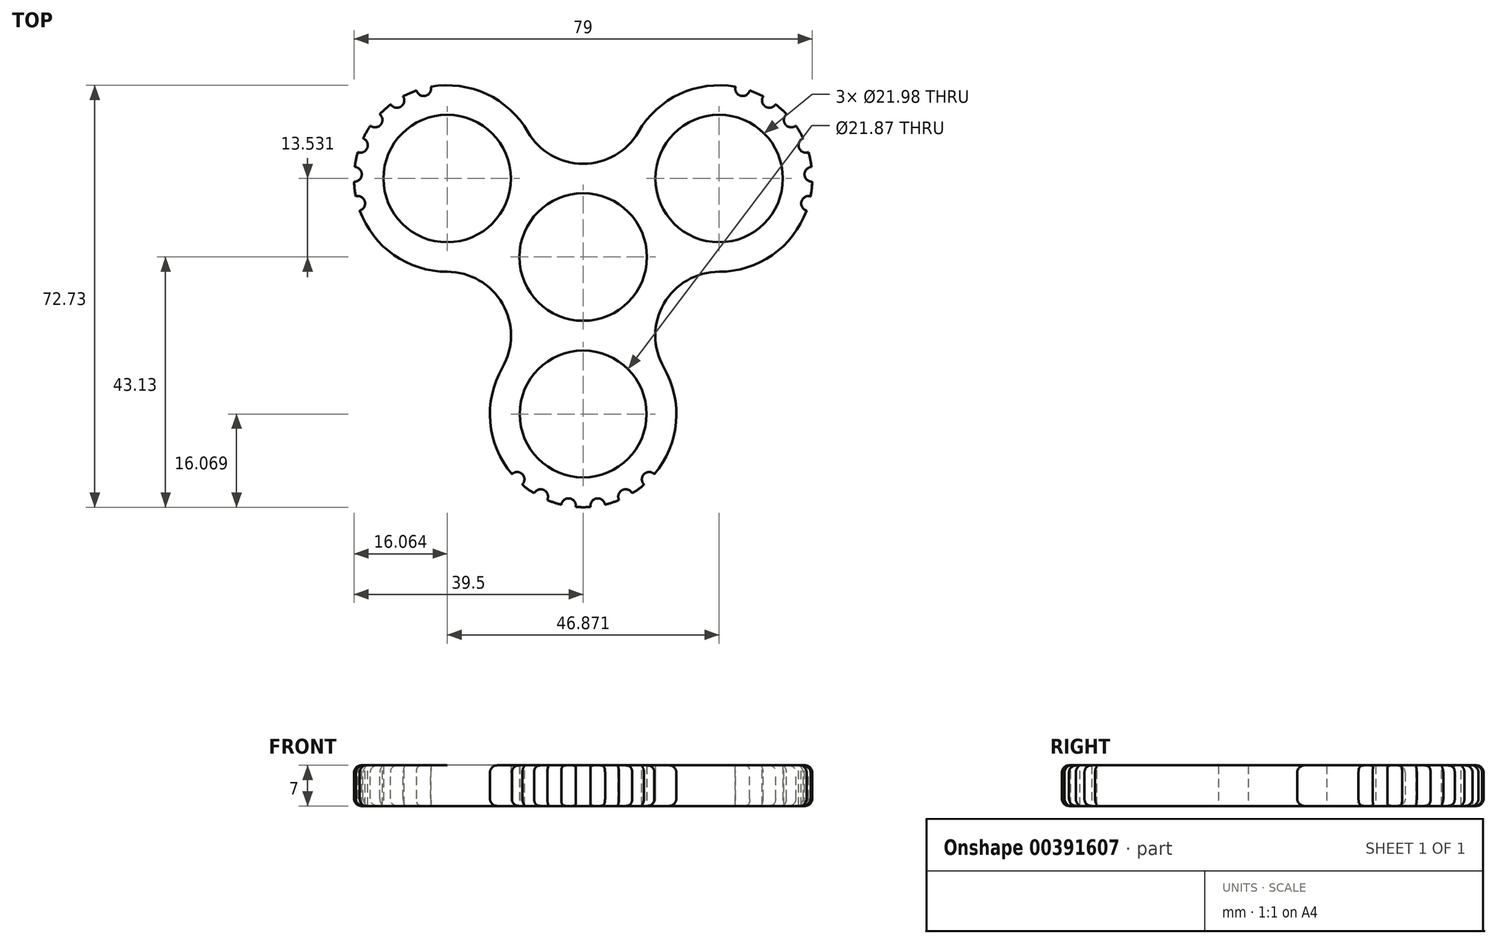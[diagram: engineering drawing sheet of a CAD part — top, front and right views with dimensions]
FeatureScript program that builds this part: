
annotation { "Feature Type Name" : "Feature", "Feature Type Description" : "" }
export const myFeature = defineFeature(function(context is Context, id is Id, definition is map)
    precondition{}
    {
        {
            var Q0;
            Q0=qCreatedBy(makeId("Top.planeOp"),FACE);
            var sketch = newSketch(context, id + "F0", { "sketchPlane" : qUnion([Q0])});
            skArc(sketch, "E0", {"start": v(0, 11) * mm, "mid": v(-5.5, -9.52) * mm, "end": v(9.52, 5.5) * mm, "construction": true});
            skLineSegment(sketch, "E1", {"start": v(0, 0) * mm, "end": v(92.12, 53.18) * mm, "construction": true});
            skLineSegment(sketch, "E2", {"start": v(0, 0) * mm, "end": v(-9.52, 5.5) * mm, "construction": true});
            skLineSegment(sketch, "E3", {"start": v(0, 0) * mm, "end": v(0, -70.87) * mm, "construction": true});
            skCircle(sketch, "E4", {"center": v(-23.44, 13.53) * mm, "radius": 11 * mm, "construction": true});
            skArc(sketch, "E5", {"start": v(13.92, 8.04) * mm, "mid": v(28.93, 4.01) * mm, "end": v(32.95, 19.03) * mm, "construction": true});
            skCircle(sketch, "E6", {"center": v(0, -27.06) * mm, "radius": 11 * mm, "construction": true});
            skLineSegment(sketch, "E7", {"start": v(0, 0) * mm, "end": v(-69.62, -40.2) * mm, "construction": true});
            skLineSegment(sketch, "E8", {"start": v(0, 0) * mm, "end": v(71.9, -41.52) * mm, "construction": true});
            skLineSegment(sketch, "E9", {"start": v(0, 0) * mm, "end": v(0, 11) * mm, "construction": true});
            skLineSegment(sketch, "E10", {"start": v(-23.44, 13.53) * mm, "end": v(-12.14, 33.1) * mm, "construction": true});
            skLineSegment(sketch, "E11", {"start": v(23.44, 13.53) * mm, "end": v(12.02, 33.3) * mm, "construction": true});
            skLineSegment(sketch, "E12", {"start": v(-37.35, 21.57) * mm, "end": v(-32.95, 19.03) * mm, "construction": true});
            skLineSegment(sketch, "E13", {"start": v(9.52, 5.5) * mm, "end": v(13.92, 8.04) * mm});
            skLineSegment(sketch, "E14", {"start": v(37.35, 21.57) * mm, "end": v(32.95, 19.03) * mm});
            skArc(sketch, "E15", {"start": v(-9.52, 5.5) * mm, "mid": v(-5.5, 9.52) * mm, "end": v(0, 11) * mm});
            skArc(sketch, "E16", {"start": v(-9.52, 21.57) * mm, "mid": v(-5.5, 17.54) * mm, "end": v(0, 16.07) * mm});
            skArc(sketch, "E17", {"start": v(-32.95, 19.03) * mm, "mid": v(-17.94, 23.05) * mm, "end": v(-13.92, 8.04) * mm});
            skLineSegment(sketch, "E18.trimOffspring", {"start": v(-37.35, 21.57) * mm, "end": v(-92.12, 53.18) * mm, "construction": true});
            skLineSegment(sketch, "E19.trimOffspring", {"start": v(-13.92, 8.04) * mm, "end": v(-32.95, 19.03) * mm, "construction": true});
            skArc(sketch, "E20", {"start": v(-9.52, 21.57) * mm, "mid": v(-23.44, 29.6) * mm, "end": v(-37.35, 21.57) * mm});
            skLineSegment(sketch, "E21", {"start": v(-37.35, 21.57) * mm, "end": v(-32.95, 19.03) * mm});
            skLineSegment(sketch, "E22", {"start": v(-13.92, 8.04) * mm, "end": v(-9.52, 5.5) * mm});
            skPoint(sketch, "E23.start.orphan", {"position": v(23.44, 29.6) * mm});
            skLineSegment(sketch, "E24.trimOffspring", {"start": v(0, 16.07) * mm, "end": v(0, 62.86) * mm, "construction": true});
            skLineSegment(sketch, "E25", {"start": v(0, 16.07) * mm, "end": v(0, 11) * mm});
            skLineSegment(sketch, "E26.MirrorCS", {"start": v(-13.92, -8.04) * mm, "end": v(-9.52, -5.5) * mm});
            skArc(sketch, "E27.MirrorCS", {"start": v(-23.44, -2.54) * mm, "mid": v(-17.94, -4.01) * mm, "end": v(-13.92, -8.04) * mm});
            skArc(sketch, "E28.MirrorCS", {"start": v(-23.44, -2.54) * mm, "mid": v(-37.35, 5.5) * mm, "end": v(-37.35, 21.57) * mm});
            skArc(sketch, "E29.MirrorCS", {"start": v(-9.52, 5.5) * mm, "mid": v(-11, 0) * mm, "end": v(-9.52, -5.5) * mm});
            skArc(sketch, "E30.MirrorCS", {"start": v(-32.95, 19.03) * mm, "mid": v(-28.93, 4.01) * mm, "end": v(-13.92, 8.04) * mm});
            skArc(sketch, "E31.MirrorCS", {"start": v(23.44, -2.54) * mm, "mid": v(37.35, 5.5) * mm, "end": v(37.35, 21.57) * mm});
            skLineSegment(sketch, "E32.MirrorCS", {"start": v(13.92, 8.04) * mm, "end": v(9.52, 5.5) * mm});
            skArc(sketch, "E33.MirrorCS", {"start": v(32.95, 19.03) * mm, "mid": v(17.94, 23.05) * mm, "end": v(13.92, 8.04) * mm});
            skArc(sketch, "E34.MirrorCS", {"start": v(32.95, 19.03) * mm, "mid": v(28.93, 4.01) * mm, "end": v(13.92, 8.04) * mm});
            skLineSegment(sketch, "E35.MirrorCS", {"start": v(13.92, -8.04) * mm, "end": v(9.52, -5.5) * mm});
            skArc(sketch, "E36.MirrorCS", {"start": v(23.44, -2.54) * mm, "mid": v(17.94, -4.01) * mm, "end": v(13.92, -8.04) * mm});
            skLineSegment(sketch, "E37.MirrorCS", {"start": v(37.35, 21.57) * mm, "end": v(32.95, 19.03) * mm, "construction": true});
            skArc(sketch, "E38.MirrorCS", {"start": v(9.52, 5.5) * mm, "mid": v(11, 0) * mm, "end": v(9.52, -5.5) * mm});
            skArc(sketch, "E39.MirrorCS", {"start": v(9.52, 21.57) * mm, "mid": v(23.44, 29.6) * mm, "end": v(37.35, 21.57) * mm});
            skLineSegment(sketch, "E40.MirrorCS", {"start": v(23.44, 13.53) * mm, "end": v(12.14, 33.1) * mm, "construction": true});
            skLineSegment(sketch, "E41.MirrorCS", {"start": v(0, 0) * mm, "end": v(9.52, 5.5) * mm, "construction": true});
            skArc(sketch, "E42.MirrorCS", {"start": v(9.52, 5.5) * mm, "mid": v(5.5, 9.52) * mm, "end": v(0, 11) * mm});
            skArc(sketch, "E43.MirrorCS", {"start": v(9.52, 21.57) * mm, "mid": v(5.5, 17.54) * mm, "end": v(0, 16.07) * mm});
            skCircle(sketch, "E44.MirrorC", {"center": v(23.44, 13.53) * mm, "radius": 11 * mm, "construction": true});
            skLineSegment(sketch, "E45.MirrorCS", {"start": v(13.92, 8.04) * mm, "end": v(32.95, 19.03) * mm, "construction": true});
            skArc(sketch, "E46", {"start": v(-9.52, -5.5) * mm, "mid": v(0, -11) * mm, "end": v(9.52, -5.5) * mm});
            skArc(sketch, "E47.MirrorCS", {"start": v(-13.92, -19.03) * mm, "mid": v(-12.45, -13.53) * mm, "end": v(-13.92, -8.04) * mm});
            skArc(sketch, "E48.MirrorCS", {"start": v(-13.92, -19.03) * mm, "mid": v(-13.92, -35.1) * mm, "end": v(0, -43.13) * mm});
            skArc(sketch, "E49.MirrorCS", {"start": v(13.92, -19.03) * mm, "mid": v(12.45, -13.53) * mm, "end": v(13.92, -8.04) * mm});
            skArc(sketch, "E50.MirrorCS", {"start": v(13.92, -19.03) * mm, "mid": v(13.92, -35.1) * mm, "end": v(0, -43.13) * mm});
            skCircle(sketch, "E51", {"center": v(0, -27.06) * mm, "radius": 10.94 * mm});
            skSolve(sketch);
        }
        {
            var Q0;
            Q0 = qSketchRegion(id + "F0", true);
            extrude(context, id + "F1", {"entities" : qUnion([Q0]), "depth" : 7 * mm});
        }
        {
            var Q0;
            Q0=makeQuery(id+"F1.opExtrude","CAP_FACE",FACE,{"disambiguationData":[OSD([sQuery(id+"F0.wireOp",EDGE,"E15"),sQuery(id+"F0.wireOp",EDGE,"E16"),sQuery(id+"F0.wireOp",EDGE,"E17"),sQuery(id+"F0.wireOp",EDGE,"E20"),sQuery(id+"F0.wireOp",EDGE,"E27.MirrorCS"),sQuery(id+"F0.wireOp",EDGE,"E29.MirrorCS"),sQuery(id+"F0.wireOp",EDGE,"E30.MirrorCS"),sQuery(id+"F0.wireOp",EDGE,"E28.MirrorCS"),sQuery(id+"F0.wireOp",EDGE,"E33.MirrorCS"),sQuery(id+"F0.wireOp",EDGE,"E34.MirrorCS"),sQuery(id+"F0.wireOp",EDGE,"E31.MirrorCS"),sQuery(id+"F0.wireOp",EDGE,"E36.MirrorCS"),sQuery(id+"F0.wireOp",EDGE,"E38.MirrorCS"),sQuery(id+"F0.wireOp",EDGE,"E39.MirrorCS"),sQuery(id+"F0.wireOp",EDGE,"E42.MirrorCS"),sQuery(id+"F0.wireOp",EDGE,"E43.MirrorCS"),sQuery(id+"F0.wireOp",EDGE,"E46"),sQuery(id+"F0.wireOp",EDGE,"E47.MirrorCS"),sQuery(id+"F0.wireOp",EDGE,"E48.MirrorCS"),sQuery(id+"F0.wireOp",EDGE,"E49.MirrorCS"),sQuery(id+"F0.wireOp",EDGE,"E50.MirrorCS"),sQuery(id+"F0.wireOp",EDGE,"E51")])],"isStart":false});
            var sketch = newSketch(context, id + "F2", { "sketchPlane" : qUnion([Q0])});
            skArc(sketch, "E52", {"start": v(-36.68, 22.64) * mm, "mid": v(-34.89, 22.83) * mm, "end": v(-35.07, 24.61) * mm});
            skArc(sketch, "E53", {"start": v(-38.85, 18.07) * mm, "mid": v(-37.21, 18.8) * mm, "end": v(-37.94, 20.44) * mm});
            skArc(sketch, "E54", {"start": v(-36.68, 22.64) * mm, "mid": v(-35.91, 23.66) * mm, "end": v(-35.07, 24.61) * mm});
            skArc(sketch, "E55", {"start": v(-38.85, 18.07) * mm, "mid": v(-38.45, 19.27) * mm, "end": v(-37.94, 20.44) * mm});
            skArc(sketch, "E56", {"start": v(-39.5, 12.99) * mm, "mid": v(-38.17, 14.2) * mm, "end": v(-39.38, 15.53) * mm});
            skArc(sketch, "E57", {"start": v(-33.18, 26.3) * mm, "mid": v(-31.43, 25.93) * mm, "end": v(-31.05, 27.68) * mm});
            skArc(sketch, "E58", {"start": v(-33.18, 26.3) * mm, "mid": v(-32.14, 27.04) * mm, "end": v(-31.05, 27.68) * mm});
            skArc(sketch, "E59", {"start": v(-39.5, 12.99) * mm, "mid": v(-39.49, 14.26) * mm, "end": v(-39.38, 15.53) * mm});
            skArc(sketch, "E60", {"start": v(-38.53, 8.02) * mm, "mid": v(-37.65, 9.58) * mm, "end": v(-39.21, 10.47) * mm});
            skArc(sketch, "E61", {"start": v(-28.72, 28.7) * mm, "mid": v(-27.17, 27.8) * mm, "end": v(-26.27, 29.35) * mm});
            skArc(sketch, "E62", {"start": v(-28.72, 28.7) * mm, "mid": v(-27.5, 29.08) * mm, "end": v(-26.27, 29.35) * mm});
            skArc(sketch, "E63", {"start": v(-38.53, 8.02) * mm, "mid": v(-38.92, 9.23) * mm, "end": v(-39.21, 10.47) * mm});
            skLineSegment(sketch, "E64", {"start": v(0, 53.35) * mm, "end": v(0, -27.06) * mm, "construction": true});
            skArc(sketch, "E65.MirrorCS", {"start": v(28.72, 28.7) * mm, "mid": v(27.17, 27.8) * mm, "end": v(26.27, 29.35) * mm});
            skArc(sketch, "E66.MirrorCS", {"start": v(28.72, 28.7) * mm, "mid": v(27.5, 29.08) * mm, "end": v(26.27, 29.35) * mm});
            skArc(sketch, "E67.MirrorCS", {"start": v(33.18, 26.3) * mm, "mid": v(31.43, 25.93) * mm, "end": v(31.05, 27.68) * mm});
            skArc(sketch, "E68.MirrorCS", {"start": v(33.18, 26.3) * mm, "mid": v(32.14, 27.04) * mm, "end": v(31.05, 27.68) * mm});
            skArc(sketch, "E69.MirrorCS", {"start": v(36.68, 22.64) * mm, "mid": v(34.89, 22.83) * mm, "end": v(35.07, 24.61) * mm});
            skArc(sketch, "E70.MirrorCS", {"start": v(38.85, 18.07) * mm, "mid": v(37.21, 18.8) * mm, "end": v(37.94, 20.44) * mm});
            skArc(sketch, "E71.MirrorCS", {"start": v(39.5, 12.99) * mm, "mid": v(38.17, 14.2) * mm, "end": v(39.38, 15.53) * mm});
            skArc(sketch, "E72.MirrorCS", {"start": v(38.53, 8.02) * mm, "mid": v(37.65, 9.58) * mm, "end": v(39.21, 10.47) * mm});
            skArc(sketch, "E73.MirrorCS", {"start": v(36.68, 22.64) * mm, "mid": v(35.91, 23.66) * mm, "end": v(35.07, 24.61) * mm});
            skArc(sketch, "E74.MirrorCS", {"start": v(38.85, 18.07) * mm, "mid": v(38.45, 19.27) * mm, "end": v(37.94, 20.44) * mm});
            skArc(sketch, "E75.MirrorCS", {"start": v(39.5, 12.99) * mm, "mid": v(39.49, 14.26) * mm, "end": v(39.38, 15.53) * mm});
            skArc(sketch, "E76.MirrorCS", {"start": v(38.53, 8.02) * mm, "mid": v(38.92, 9.23) * mm, "end": v(39.21, 10.47) * mm});
            skArc(sketch, "E77", {"start": v(3.78, -42.68) * mm, "mid": v(2.32, -41.63) * mm, "end": v(1.27, -43.08) * mm});
            skArc(sketch, "E78", {"start": v(8.45, -40.73) * mm, "mid": v(6.74, -40.18) * mm, "end": v(6.2, -41.9) * mm});
            skArc(sketch, "E79", {"start": v(12.28, -37.42) * mm, "mid": v(10.49, -37.43) * mm, "end": v(10.5, -39.23) * mm});
            skArc(sketch, "E80", {"start": v(-1.27, -43.08) * mm, "mid": v(-2.32, -41.63) * mm, "end": v(-3.78, -42.68) * mm});
            skArc(sketch, "E81", {"start": v(-6.2, -41.9) * mm, "mid": v(-6.74, -40.18) * mm, "end": v(-8.45, -40.73) * mm});
            skArc(sketch, "E82", {"start": v(-10.5, -39.23) * mm, "mid": v(-10.49, -37.43) * mm, "end": v(-12.28, -37.42) * mm});
            skArc(sketch, "E83", {"start": v(12.28, -37.42) * mm, "mid": v(11.43, -38.36) * mm, "end": v(10.5, -39.23) * mm});
            skArc(sketch, "E84", {"start": v(8.45, -40.73) * mm, "mid": v(7.34, -41.36) * mm, "end": v(6.2, -41.9) * mm});
            skArc(sketch, "E85", {"start": v(3.78, -42.68) * mm, "mid": v(2.53, -42.93) * mm, "end": v(1.27, -43.08) * mm});
            skArc(sketch, "E86", {"start": v(-1.27, -43.08) * mm, "mid": v(-2.53, -42.93) * mm, "end": v(-3.78, -42.68) * mm});
            skArc(sketch, "E87", {"start": v(-6.2, -41.9) * mm, "mid": v(-7.34, -41.36) * mm, "end": v(-8.45, -40.73) * mm});
            skArc(sketch, "E88", {"start": v(-10.5, -39.23) * mm, "mid": v(-11.43, -38.36) * mm, "end": v(-12.28, -37.42) * mm});
            skSolve(sketch);
        }
        {
            var Q0;
            Q0 = qSketchRegion(id + "F2", true);
            extrude(context, id + "F3", {"entities" : qUnion([Q0]), "operationType" : NewBodyOperationType.REMOVE, "endBound" : BoundingType.THROUGH_ALL, "oppositeDirection" : true, "depth" : 25.4 * mm});
        }
        {
            var Q0;
            {var subQ0=sQuery(id+"F0.wireOp",EDGE,"E47.MirrorCS");var subQ1=sQuery(id+"F0.wireOp",EDGE,"E28.MirrorCS");var subQ2=sQuery(id+"F0.wireOp",EDGE,"E27.MirrorCS");var subQ3=sQuery(id+"F0.wireOp",EDGE,"E20");Q0=makeQuery(id+"F3.boolean.opBoolean","SPLIT",EDGE,{"disambiguationData":[TD([makeQuery(id+"F1.opExtrude","CAP_FACE",FACE,{"disambiguationData":[OSD([sQuery(id+"F0.wireOp",EDGE,"E15"),sQuery(id+"F0.wireOp",EDGE,"E16"),sQuery(id+"F0.wireOp",EDGE,"E17"),subQ3,subQ2,sQuery(id+"F0.wireOp",EDGE,"E29.MirrorCS"),sQuery(id+"F0.wireOp",EDGE,"E30.MirrorCS"),subQ1,sQuery(id+"F0.wireOp",EDGE,"E33.MirrorCS"),sQuery(id+"F0.wireOp",EDGE,"E34.MirrorCS"),sQuery(id+"F0.wireOp",EDGE,"E31.MirrorCS"),sQuery(id+"F0.wireOp",EDGE,"E36.MirrorCS"),sQuery(id+"F0.wireOp",EDGE,"E38.MirrorCS"),sQuery(id+"F0.wireOp",EDGE,"E39.MirrorCS"),sQuery(id+"F0.wireOp",EDGE,"E42.MirrorCS"),sQuery(id+"F0.wireOp",EDGE,"E43.MirrorCS"),sQuery(id+"F0.wireOp",EDGE,"E46"),subQ0,sQuery(id+"F0.wireOp",EDGE,"E48.MirrorCS"),sQuery(id+"F0.wireOp",EDGE,"E49.MirrorCS"),sQuery(id+"F0.wireOp",EDGE,"E50.MirrorCS"),sQuery(id+"F0.wireOp",EDGE,"E51")])],"isStart":false}),makeQuery(id+"F1.opExtrude","SWEPT_FACE",FACE,{"disambiguationData":[OSD([subQ3,subQ1])]}),makeQuery(id+"F1.opExtrude","SWEPT_FACE",FACE,{"disambiguationData":[OSD([subQ2,subQ0])]}),makeQuery(id+"F3.opExtrude","SWEPT_FACE",FACE,{"disambiguationData":[OSD([sQuery(id+"F2.wireOp",EDGE,"E60")])]})])],"derivedFrom":makeQuery(id+"F1.opExtrude","CAP_EDGE",EDGE,{"disambiguationData":[OSD([subQ3,subQ1])],"isStart":false})});}
            var Q1;
            Q1=makeQuery(id+"F1.opExtrude","CAP_EDGE",EDGE,{"disambiguationData":[OSD([sQuery(id+"F0.wireOp",EDGE,"E27.MirrorCS"),sQuery(id+"F0.wireOp",EDGE,"E47.MirrorCS")])],"isStart":false});
            var Q2;
            {var subQ0=sQuery(id+"F0.wireOp",EDGE,"E50.MirrorCS");var subQ1=sQuery(id+"F0.wireOp",EDGE,"E48.MirrorCS");var subQ2=sQuery(id+"F0.wireOp",EDGE,"E47.MirrorCS");var subQ3=sQuery(id+"F0.wireOp",EDGE,"E27.MirrorCS");Q2=makeQuery(id+"F3.boolean.opBoolean","SPLIT",EDGE,{"disambiguationData":[TD([makeQuery(id+"F1.opExtrude","CAP_FACE",FACE,{"disambiguationData":[OSD([sQuery(id+"F0.wireOp",EDGE,"E15"),sQuery(id+"F0.wireOp",EDGE,"E16"),sQuery(id+"F0.wireOp",EDGE,"E17"),sQuery(id+"F0.wireOp",EDGE,"E20"),subQ3,sQuery(id+"F0.wireOp",EDGE,"E29.MirrorCS"),sQuery(id+"F0.wireOp",EDGE,"E30.MirrorCS"),sQuery(id+"F0.wireOp",EDGE,"E28.MirrorCS"),sQuery(id+"F0.wireOp",EDGE,"E33.MirrorCS"),sQuery(id+"F0.wireOp",EDGE,"E34.MirrorCS"),sQuery(id+"F0.wireOp",EDGE,"E31.MirrorCS"),sQuery(id+"F0.wireOp",EDGE,"E36.MirrorCS"),sQuery(id+"F0.wireOp",EDGE,"E38.MirrorCS"),sQuery(id+"F0.wireOp",EDGE,"E39.MirrorCS"),sQuery(id+"F0.wireOp",EDGE,"E42.MirrorCS"),sQuery(id+"F0.wireOp",EDGE,"E43.MirrorCS"),sQuery(id+"F0.wireOp",EDGE,"E46"),subQ2,subQ1,sQuery(id+"F0.wireOp",EDGE,"E49.MirrorCS"),subQ0,sQuery(id+"F0.wireOp",EDGE,"E51")])],"isStart":false}),makeQuery(id+"F1.opExtrude","SWEPT_FACE",FACE,{"disambiguationData":[OSD([subQ3,subQ2])]}),makeQuery(id+"F1.opExtrude","SWEPT_FACE",FACE,{"disambiguationData":[OSD([subQ1,subQ0])]}),makeQuery(id+"F3.opExtrude","SWEPT_FACE",FACE,{"disambiguationData":[OSD([sQuery(id+"F2.wireOp",EDGE,"E82")])]})])],"derivedFrom":makeQuery(id+"F1.opExtrude","CAP_EDGE",EDGE,{"disambiguationData":[OSD([subQ1,subQ0])],"isStart":false})});}
            var Q3;
            {var subQ0=sQuery(id+"F0.wireOp",EDGE,"E50.MirrorCS");var subQ1=sQuery(id+"F0.wireOp",EDGE,"E49.MirrorCS");var subQ2=sQuery(id+"F0.wireOp",EDGE,"E48.MirrorCS");var subQ3=sQuery(id+"F0.wireOp",EDGE,"E36.MirrorCS");Q3=makeQuery(id+"F3.boolean.opBoolean","SPLIT",EDGE,{"disambiguationData":[TD([makeQuery(id+"F1.opExtrude","CAP_FACE",FACE,{"disambiguationData":[OSD([sQuery(id+"F0.wireOp",EDGE,"E15"),sQuery(id+"F0.wireOp",EDGE,"E16"),sQuery(id+"F0.wireOp",EDGE,"E17"),sQuery(id+"F0.wireOp",EDGE,"E20"),sQuery(id+"F0.wireOp",EDGE,"E27.MirrorCS"),sQuery(id+"F0.wireOp",EDGE,"E29.MirrorCS"),sQuery(id+"F0.wireOp",EDGE,"E30.MirrorCS"),sQuery(id+"F0.wireOp",EDGE,"E28.MirrorCS"),sQuery(id+"F0.wireOp",EDGE,"E33.MirrorCS"),sQuery(id+"F0.wireOp",EDGE,"E34.MirrorCS"),sQuery(id+"F0.wireOp",EDGE,"E31.MirrorCS"),subQ3,sQuery(id+"F0.wireOp",EDGE,"E38.MirrorCS"),sQuery(id+"F0.wireOp",EDGE,"E39.MirrorCS"),sQuery(id+"F0.wireOp",EDGE,"E42.MirrorCS"),sQuery(id+"F0.wireOp",EDGE,"E43.MirrorCS"),sQuery(id+"F0.wireOp",EDGE,"E46"),sQuery(id+"F0.wireOp",EDGE,"E47.MirrorCS"),subQ2,subQ1,subQ0,sQuery(id+"F0.wireOp",EDGE,"E51")])],"isStart":false}),makeQuery(id+"F1.opExtrude","SWEPT_FACE",FACE,{"disambiguationData":[OSD([subQ3,subQ1])]}),makeQuery(id+"F1.opExtrude","SWEPT_FACE",FACE,{"disambiguationData":[OSD([subQ2,subQ0])]}),makeQuery(id+"F3.opExtrude","SWEPT_FACE",FACE,{"disambiguationData":[OSD([sQuery(id+"F2.wireOp",EDGE,"E79")])]})])],"derivedFrom":makeQuery(id+"F1.opExtrude","CAP_EDGE",EDGE,{"disambiguationData":[OSD([subQ2,subQ0])],"isStart":false})});}
            var Q4;
            Q4=makeQuery(id+"F1.opExtrude","CAP_EDGE",EDGE,{"disambiguationData":[OSD([sQuery(id+"F0.wireOp",EDGE,"E36.MirrorCS"),sQuery(id+"F0.wireOp",EDGE,"E49.MirrorCS")])],"isStart":false});
            var Q5;
            {var subQ0=sQuery(id+"F0.wireOp",EDGE,"E49.MirrorCS");var subQ1=sQuery(id+"F0.wireOp",EDGE,"E39.MirrorCS");var subQ2=sQuery(id+"F0.wireOp",EDGE,"E36.MirrorCS");var subQ3=sQuery(id+"F0.wireOp",EDGE,"E31.MirrorCS");Q5=makeQuery(id+"F3.boolean.opBoolean","SPLIT",EDGE,{"disambiguationData":[TD([makeQuery(id+"F1.opExtrude","CAP_FACE",FACE,{"disambiguationData":[OSD([sQuery(id+"F0.wireOp",EDGE,"E15"),sQuery(id+"F0.wireOp",EDGE,"E16"),sQuery(id+"F0.wireOp",EDGE,"E17"),sQuery(id+"F0.wireOp",EDGE,"E20"),sQuery(id+"F0.wireOp",EDGE,"E27.MirrorCS"),sQuery(id+"F0.wireOp",EDGE,"E29.MirrorCS"),sQuery(id+"F0.wireOp",EDGE,"E30.MirrorCS"),sQuery(id+"F0.wireOp",EDGE,"E28.MirrorCS"),sQuery(id+"F0.wireOp",EDGE,"E33.MirrorCS"),sQuery(id+"F0.wireOp",EDGE,"E34.MirrorCS"),subQ3,subQ2,sQuery(id+"F0.wireOp",EDGE,"E38.MirrorCS"),subQ1,sQuery(id+"F0.wireOp",EDGE,"E42.MirrorCS"),sQuery(id+"F0.wireOp",EDGE,"E43.MirrorCS"),sQuery(id+"F0.wireOp",EDGE,"E46"),sQuery(id+"F0.wireOp",EDGE,"E47.MirrorCS"),sQuery(id+"F0.wireOp",EDGE,"E48.MirrorCS"),subQ0,sQuery(id+"F0.wireOp",EDGE,"E50.MirrorCS"),sQuery(id+"F0.wireOp",EDGE,"E51")])],"isStart":false}),makeQuery(id+"F1.opExtrude","SWEPT_FACE",FACE,{"disambiguationData":[OSD([subQ3,subQ1])]}),makeQuery(id+"F1.opExtrude","SWEPT_FACE",FACE,{"disambiguationData":[OSD([subQ2,subQ0])]}),makeQuery(id+"F3.opExtrude","SWEPT_FACE",FACE,{"disambiguationData":[OSD([sQuery(id+"F2.wireOp",EDGE,"E72.MirrorCS")])]})])],"derivedFrom":makeQuery(id+"F1.opExtrude","CAP_EDGE",EDGE,{"disambiguationData":[OSD([subQ3,subQ1])],"isStart":false})});}
            var Q6;
            {var subQ0=sQuery(id+"F0.wireOp",EDGE,"E43.MirrorCS");var subQ1=sQuery(id+"F0.wireOp",EDGE,"E39.MirrorCS");var subQ2=sQuery(id+"F0.wireOp",EDGE,"E31.MirrorCS");var subQ3=sQuery(id+"F0.wireOp",EDGE,"E16");Q6=makeQuery(id+"F3.boolean.opBoolean","SPLIT",EDGE,{"disambiguationData":[TD([makeQuery(id+"F1.opExtrude","CAP_FACE",FACE,{"disambiguationData":[OSD([sQuery(id+"F0.wireOp",EDGE,"E15"),subQ3,sQuery(id+"F0.wireOp",EDGE,"E17"),sQuery(id+"F0.wireOp",EDGE,"E20"),sQuery(id+"F0.wireOp",EDGE,"E27.MirrorCS"),sQuery(id+"F0.wireOp",EDGE,"E29.MirrorCS"),sQuery(id+"F0.wireOp",EDGE,"E30.MirrorCS"),sQuery(id+"F0.wireOp",EDGE,"E28.MirrorCS"),sQuery(id+"F0.wireOp",EDGE,"E33.MirrorCS"),sQuery(id+"F0.wireOp",EDGE,"E34.MirrorCS"),subQ2,sQuery(id+"F0.wireOp",EDGE,"E36.MirrorCS"),sQuery(id+"F0.wireOp",EDGE,"E38.MirrorCS"),subQ1,sQuery(id+"F0.wireOp",EDGE,"E42.MirrorCS"),subQ0,sQuery(id+"F0.wireOp",EDGE,"E46"),sQuery(id+"F0.wireOp",EDGE,"E47.MirrorCS"),sQuery(id+"F0.wireOp",EDGE,"E48.MirrorCS"),sQuery(id+"F0.wireOp",EDGE,"E49.MirrorCS"),sQuery(id+"F0.wireOp",EDGE,"E50.MirrorCS"),sQuery(id+"F0.wireOp",EDGE,"E51")])],"isStart":false}),makeQuery(id+"F1.opExtrude","SWEPT_FACE",FACE,{"disambiguationData":[OSD([subQ3,subQ0])]}),makeQuery(id+"F1.opExtrude","SWEPT_FACE",FACE,{"disambiguationData":[OSD([subQ2,subQ1])]}),makeQuery(id+"F3.opExtrude","SWEPT_FACE",FACE,{"disambiguationData":[OSD([sQuery(id+"F2.wireOp",EDGE,"E65.MirrorCS")])]})])],"derivedFrom":makeQuery(id+"F1.opExtrude","CAP_EDGE",EDGE,{"disambiguationData":[OSD([subQ2,subQ1])],"isStart":false})});}
            var Q7;
            Q7=makeQuery(id+"F1.opExtrude","CAP_EDGE",EDGE,{"disambiguationData":[OSD([sQuery(id+"F0.wireOp",EDGE,"E16"),sQuery(id+"F0.wireOp",EDGE,"E43.MirrorCS")])],"isStart":false});
            var Q8;
            {var subQ0=sQuery(id+"F0.wireOp",EDGE,"E43.MirrorCS");var subQ1=sQuery(id+"F0.wireOp",EDGE,"E28.MirrorCS");var subQ2=sQuery(id+"F0.wireOp",EDGE,"E20");var subQ3=sQuery(id+"F0.wireOp",EDGE,"E16");Q8=makeQuery(id+"F3.boolean.opBoolean","SPLIT",EDGE,{"disambiguationData":[TD([makeQuery(id+"F1.opExtrude","CAP_FACE",FACE,{"disambiguationData":[OSD([sQuery(id+"F0.wireOp",EDGE,"E15"),subQ3,sQuery(id+"F0.wireOp",EDGE,"E17"),subQ2,sQuery(id+"F0.wireOp",EDGE,"E27.MirrorCS"),sQuery(id+"F0.wireOp",EDGE,"E29.MirrorCS"),sQuery(id+"F0.wireOp",EDGE,"E30.MirrorCS"),subQ1,sQuery(id+"F0.wireOp",EDGE,"E33.MirrorCS"),sQuery(id+"F0.wireOp",EDGE,"E34.MirrorCS"),sQuery(id+"F0.wireOp",EDGE,"E31.MirrorCS"),sQuery(id+"F0.wireOp",EDGE,"E36.MirrorCS"),sQuery(id+"F0.wireOp",EDGE,"E38.MirrorCS"),sQuery(id+"F0.wireOp",EDGE,"E39.MirrorCS"),sQuery(id+"F0.wireOp",EDGE,"E42.MirrorCS"),subQ0,sQuery(id+"F0.wireOp",EDGE,"E46"),sQuery(id+"F0.wireOp",EDGE,"E47.MirrorCS"),sQuery(id+"F0.wireOp",EDGE,"E48.MirrorCS"),sQuery(id+"F0.wireOp",EDGE,"E49.MirrorCS"),sQuery(id+"F0.wireOp",EDGE,"E50.MirrorCS"),sQuery(id+"F0.wireOp",EDGE,"E51")])],"isStart":false}),makeQuery(id+"F1.opExtrude","SWEPT_FACE",FACE,{"disambiguationData":[OSD([subQ3,subQ0])]}),makeQuery(id+"F1.opExtrude","SWEPT_FACE",FACE,{"disambiguationData":[OSD([subQ2,subQ1])]}),makeQuery(id+"F3.opExtrude","SWEPT_FACE",FACE,{"disambiguationData":[OSD([sQuery(id+"F2.wireOp",EDGE,"E61")])]})])],"derivedFrom":makeQuery(id+"F1.opExtrude","CAP_EDGE",EDGE,{"disambiguationData":[OSD([subQ2,subQ1])],"isStart":false})});}
            var Q9;
            Q9=makeQuery(id+"F1.opExtrude","CAP_EDGE",EDGE,{"disambiguationData":[OSD([sQuery(id+"F0.wireOp",EDGE,"E36.MirrorCS"),sQuery(id+"F0.wireOp",EDGE,"E49.MirrorCS")])],"isStart":true});
            var Q10;
            {var subQ0=sQuery(id+"F0.wireOp",EDGE,"E50.MirrorCS");var subQ1=sQuery(id+"F0.wireOp",EDGE,"E49.MirrorCS");var subQ2=sQuery(id+"F0.wireOp",EDGE,"E48.MirrorCS");var subQ3=sQuery(id+"F0.wireOp",EDGE,"E36.MirrorCS");Q10=makeQuery(id+"F3.boolean.opBoolean","SPLIT",EDGE,{"disambiguationData":[TD([makeQuery(id+"F1.opExtrude","CAP_FACE",FACE,{"disambiguationData":[OSD([sQuery(id+"F0.wireOp",EDGE,"E15"),sQuery(id+"F0.wireOp",EDGE,"E16"),sQuery(id+"F0.wireOp",EDGE,"E17"),sQuery(id+"F0.wireOp",EDGE,"E20"),sQuery(id+"F0.wireOp",EDGE,"E27.MirrorCS"),sQuery(id+"F0.wireOp",EDGE,"E29.MirrorCS"),sQuery(id+"F0.wireOp",EDGE,"E30.MirrorCS"),sQuery(id+"F0.wireOp",EDGE,"E28.MirrorCS"),sQuery(id+"F0.wireOp",EDGE,"E33.MirrorCS"),sQuery(id+"F0.wireOp",EDGE,"E34.MirrorCS"),sQuery(id+"F0.wireOp",EDGE,"E31.MirrorCS"),subQ3,sQuery(id+"F0.wireOp",EDGE,"E38.MirrorCS"),sQuery(id+"F0.wireOp",EDGE,"E39.MirrorCS"),sQuery(id+"F0.wireOp",EDGE,"E42.MirrorCS"),sQuery(id+"F0.wireOp",EDGE,"E43.MirrorCS"),sQuery(id+"F0.wireOp",EDGE,"E46"),sQuery(id+"F0.wireOp",EDGE,"E47.MirrorCS"),subQ2,subQ1,subQ0,sQuery(id+"F0.wireOp",EDGE,"E51")])],"isStart":true}),makeQuery(id+"F1.opExtrude","SWEPT_FACE",FACE,{"disambiguationData":[OSD([subQ3,subQ1])]}),makeQuery(id+"F1.opExtrude","SWEPT_FACE",FACE,{"disambiguationData":[OSD([subQ2,subQ0])]}),makeQuery(id+"F3.opExtrude","SWEPT_FACE",FACE,{"disambiguationData":[OSD([sQuery(id+"F2.wireOp",EDGE,"E79")])]})])],"derivedFrom":makeQuery(id+"F1.opExtrude","CAP_EDGE",EDGE,{"disambiguationData":[OSD([subQ2,subQ0])],"isStart":true})});}
            var Q11;
            {var subQ0=sQuery(id+"F0.wireOp",EDGE,"E49.MirrorCS");var subQ1=sQuery(id+"F0.wireOp",EDGE,"E39.MirrorCS");var subQ2=sQuery(id+"F0.wireOp",EDGE,"E36.MirrorCS");var subQ3=sQuery(id+"F0.wireOp",EDGE,"E31.MirrorCS");Q11=makeQuery(id+"F3.boolean.opBoolean","SPLIT",EDGE,{"disambiguationData":[TD([makeQuery(id+"F1.opExtrude","CAP_FACE",FACE,{"disambiguationData":[OSD([sQuery(id+"F0.wireOp",EDGE,"E15"),sQuery(id+"F0.wireOp",EDGE,"E16"),sQuery(id+"F0.wireOp",EDGE,"E17"),sQuery(id+"F0.wireOp",EDGE,"E20"),sQuery(id+"F0.wireOp",EDGE,"E27.MirrorCS"),sQuery(id+"F0.wireOp",EDGE,"E29.MirrorCS"),sQuery(id+"F0.wireOp",EDGE,"E30.MirrorCS"),sQuery(id+"F0.wireOp",EDGE,"E28.MirrorCS"),sQuery(id+"F0.wireOp",EDGE,"E33.MirrorCS"),sQuery(id+"F0.wireOp",EDGE,"E34.MirrorCS"),subQ3,subQ2,sQuery(id+"F0.wireOp",EDGE,"E38.MirrorCS"),subQ1,sQuery(id+"F0.wireOp",EDGE,"E42.MirrorCS"),sQuery(id+"F0.wireOp",EDGE,"E43.MirrorCS"),sQuery(id+"F0.wireOp",EDGE,"E46"),sQuery(id+"F0.wireOp",EDGE,"E47.MirrorCS"),sQuery(id+"F0.wireOp",EDGE,"E48.MirrorCS"),subQ0,sQuery(id+"F0.wireOp",EDGE,"E50.MirrorCS"),sQuery(id+"F0.wireOp",EDGE,"E51")])],"isStart":true}),makeQuery(id+"F1.opExtrude","SWEPT_FACE",FACE,{"disambiguationData":[OSD([subQ3,subQ1])]}),makeQuery(id+"F1.opExtrude","SWEPT_FACE",FACE,{"disambiguationData":[OSD([subQ2,subQ0])]}),makeQuery(id+"F3.opExtrude","SWEPT_FACE",FACE,{"disambiguationData":[OSD([sQuery(id+"F2.wireOp",EDGE,"E72.MirrorCS")])]})])],"derivedFrom":makeQuery(id+"F1.opExtrude","CAP_EDGE",EDGE,{"disambiguationData":[OSD([subQ3,subQ1])],"isStart":true})});}
            var Q12;
            {var subQ0=sQuery(id+"F0.wireOp",EDGE,"E47.MirrorCS");var subQ1=sQuery(id+"F0.wireOp",EDGE,"E28.MirrorCS");var subQ2=sQuery(id+"F0.wireOp",EDGE,"E27.MirrorCS");var subQ3=sQuery(id+"F0.wireOp",EDGE,"E20");Q12=makeQuery(id+"F3.boolean.opBoolean","SPLIT",EDGE,{"disambiguationData":[TD([makeQuery(id+"F1.opExtrude","CAP_FACE",FACE,{"disambiguationData":[OSD([sQuery(id+"F0.wireOp",EDGE,"E15"),sQuery(id+"F0.wireOp",EDGE,"E16"),sQuery(id+"F0.wireOp",EDGE,"E17"),subQ3,subQ2,sQuery(id+"F0.wireOp",EDGE,"E29.MirrorCS"),sQuery(id+"F0.wireOp",EDGE,"E30.MirrorCS"),subQ1,sQuery(id+"F0.wireOp",EDGE,"E33.MirrorCS"),sQuery(id+"F0.wireOp",EDGE,"E34.MirrorCS"),sQuery(id+"F0.wireOp",EDGE,"E31.MirrorCS"),sQuery(id+"F0.wireOp",EDGE,"E36.MirrorCS"),sQuery(id+"F0.wireOp",EDGE,"E38.MirrorCS"),sQuery(id+"F0.wireOp",EDGE,"E39.MirrorCS"),sQuery(id+"F0.wireOp",EDGE,"E42.MirrorCS"),sQuery(id+"F0.wireOp",EDGE,"E43.MirrorCS"),sQuery(id+"F0.wireOp",EDGE,"E46"),subQ0,sQuery(id+"F0.wireOp",EDGE,"E48.MirrorCS"),sQuery(id+"F0.wireOp",EDGE,"E49.MirrorCS"),sQuery(id+"F0.wireOp",EDGE,"E50.MirrorCS"),sQuery(id+"F0.wireOp",EDGE,"E51")])],"isStart":true}),makeQuery(id+"F1.opExtrude","SWEPT_FACE",FACE,{"disambiguationData":[OSD([subQ3,subQ1])]}),makeQuery(id+"F1.opExtrude","SWEPT_FACE",FACE,{"disambiguationData":[OSD([subQ2,subQ0])]}),makeQuery(id+"F3.opExtrude","SWEPT_FACE",FACE,{"disambiguationData":[OSD([sQuery(id+"F2.wireOp",EDGE,"E60")])]})])],"derivedFrom":makeQuery(id+"F1.opExtrude","CAP_EDGE",EDGE,{"disambiguationData":[OSD([subQ3,subQ1])],"isStart":true})});}
            var Q13;
            Q13=makeQuery(id+"F1.opExtrude","CAP_EDGE",EDGE,{"disambiguationData":[OSD([sQuery(id+"F0.wireOp",EDGE,"E27.MirrorCS"),sQuery(id+"F0.wireOp",EDGE,"E47.MirrorCS")])],"isStart":true});
            var Q14;
            {var subQ0=sQuery(id+"F0.wireOp",EDGE,"E50.MirrorCS");var subQ1=sQuery(id+"F0.wireOp",EDGE,"E48.MirrorCS");var subQ2=sQuery(id+"F0.wireOp",EDGE,"E47.MirrorCS");var subQ3=sQuery(id+"F0.wireOp",EDGE,"E27.MirrorCS");Q14=makeQuery(id+"F3.boolean.opBoolean","SPLIT",EDGE,{"disambiguationData":[TD([makeQuery(id+"F1.opExtrude","CAP_FACE",FACE,{"disambiguationData":[OSD([sQuery(id+"F0.wireOp",EDGE,"E15"),sQuery(id+"F0.wireOp",EDGE,"E16"),sQuery(id+"F0.wireOp",EDGE,"E17"),sQuery(id+"F0.wireOp",EDGE,"E20"),subQ3,sQuery(id+"F0.wireOp",EDGE,"E29.MirrorCS"),sQuery(id+"F0.wireOp",EDGE,"E30.MirrorCS"),sQuery(id+"F0.wireOp",EDGE,"E28.MirrorCS"),sQuery(id+"F0.wireOp",EDGE,"E33.MirrorCS"),sQuery(id+"F0.wireOp",EDGE,"E34.MirrorCS"),sQuery(id+"F0.wireOp",EDGE,"E31.MirrorCS"),sQuery(id+"F0.wireOp",EDGE,"E36.MirrorCS"),sQuery(id+"F0.wireOp",EDGE,"E38.MirrorCS"),sQuery(id+"F0.wireOp",EDGE,"E39.MirrorCS"),sQuery(id+"F0.wireOp",EDGE,"E42.MirrorCS"),sQuery(id+"F0.wireOp",EDGE,"E43.MirrorCS"),sQuery(id+"F0.wireOp",EDGE,"E46"),subQ2,subQ1,sQuery(id+"F0.wireOp",EDGE,"E49.MirrorCS"),subQ0,sQuery(id+"F0.wireOp",EDGE,"E51")])],"isStart":true}),makeQuery(id+"F1.opExtrude","SWEPT_FACE",FACE,{"disambiguationData":[OSD([subQ3,subQ2])]}),makeQuery(id+"F1.opExtrude","SWEPT_FACE",FACE,{"disambiguationData":[OSD([subQ1,subQ0])]}),makeQuery(id+"F3.opExtrude","SWEPT_FACE",FACE,{"disambiguationData":[OSD([sQuery(id+"F2.wireOp",EDGE,"E82")])]})])],"derivedFrom":makeQuery(id+"F1.opExtrude","CAP_EDGE",EDGE,{"disambiguationData":[OSD([subQ1,subQ0])],"isStart":true})});}
            var Q15;
            {var subQ0=sQuery(id+"F0.wireOp",EDGE,"E43.MirrorCS");var subQ1=sQuery(id+"F0.wireOp",EDGE,"E28.MirrorCS");var subQ2=sQuery(id+"F0.wireOp",EDGE,"E20");var subQ3=sQuery(id+"F0.wireOp",EDGE,"E16");Q15=makeQuery(id+"F3.boolean.opBoolean","SPLIT",EDGE,{"disambiguationData":[TD([makeQuery(id+"F1.opExtrude","CAP_FACE",FACE,{"disambiguationData":[OSD([sQuery(id+"F0.wireOp",EDGE,"E15"),subQ3,sQuery(id+"F0.wireOp",EDGE,"E17"),subQ2,sQuery(id+"F0.wireOp",EDGE,"E27.MirrorCS"),sQuery(id+"F0.wireOp",EDGE,"E29.MirrorCS"),sQuery(id+"F0.wireOp",EDGE,"E30.MirrorCS"),subQ1,sQuery(id+"F0.wireOp",EDGE,"E33.MirrorCS"),sQuery(id+"F0.wireOp",EDGE,"E34.MirrorCS"),sQuery(id+"F0.wireOp",EDGE,"E31.MirrorCS"),sQuery(id+"F0.wireOp",EDGE,"E36.MirrorCS"),sQuery(id+"F0.wireOp",EDGE,"E38.MirrorCS"),sQuery(id+"F0.wireOp",EDGE,"E39.MirrorCS"),sQuery(id+"F0.wireOp",EDGE,"E42.MirrorCS"),subQ0,sQuery(id+"F0.wireOp",EDGE,"E46"),sQuery(id+"F0.wireOp",EDGE,"E47.MirrorCS"),sQuery(id+"F0.wireOp",EDGE,"E48.MirrorCS"),sQuery(id+"F0.wireOp",EDGE,"E49.MirrorCS"),sQuery(id+"F0.wireOp",EDGE,"E50.MirrorCS"),sQuery(id+"F0.wireOp",EDGE,"E51")])],"isStart":true}),makeQuery(id+"F1.opExtrude","SWEPT_FACE",FACE,{"disambiguationData":[OSD([subQ3,subQ0])]}),makeQuery(id+"F1.opExtrude","SWEPT_FACE",FACE,{"disambiguationData":[OSD([subQ2,subQ1])]}),makeQuery(id+"F3.opExtrude","SWEPT_FACE",FACE,{"disambiguationData":[OSD([sQuery(id+"F2.wireOp",EDGE,"E61")])]})])],"derivedFrom":makeQuery(id+"F1.opExtrude","CAP_EDGE",EDGE,{"disambiguationData":[OSD([subQ2,subQ1])],"isStart":true})});}
            var Q16;
            Q16=makeQuery(id+"F1.opExtrude","CAP_EDGE",EDGE,{"disambiguationData":[OSD([sQuery(id+"F0.wireOp",EDGE,"E16"),sQuery(id+"F0.wireOp",EDGE,"E43.MirrorCS")])],"isStart":true});
            var Q17;
            {var subQ0=sQuery(id+"F0.wireOp",EDGE,"E43.MirrorCS");var subQ1=sQuery(id+"F0.wireOp",EDGE,"E39.MirrorCS");var subQ2=sQuery(id+"F0.wireOp",EDGE,"E31.MirrorCS");var subQ3=sQuery(id+"F0.wireOp",EDGE,"E16");Q17=makeQuery(id+"F3.boolean.opBoolean","SPLIT",EDGE,{"disambiguationData":[TD([makeQuery(id+"F1.opExtrude","CAP_FACE",FACE,{"disambiguationData":[OSD([sQuery(id+"F0.wireOp",EDGE,"E15"),subQ3,sQuery(id+"F0.wireOp",EDGE,"E17"),sQuery(id+"F0.wireOp",EDGE,"E20"),sQuery(id+"F0.wireOp",EDGE,"E27.MirrorCS"),sQuery(id+"F0.wireOp",EDGE,"E29.MirrorCS"),sQuery(id+"F0.wireOp",EDGE,"E30.MirrorCS"),sQuery(id+"F0.wireOp",EDGE,"E28.MirrorCS"),sQuery(id+"F0.wireOp",EDGE,"E33.MirrorCS"),sQuery(id+"F0.wireOp",EDGE,"E34.MirrorCS"),subQ2,sQuery(id+"F0.wireOp",EDGE,"E36.MirrorCS"),sQuery(id+"F0.wireOp",EDGE,"E38.MirrorCS"),subQ1,sQuery(id+"F0.wireOp",EDGE,"E42.MirrorCS"),subQ0,sQuery(id+"F0.wireOp",EDGE,"E46"),sQuery(id+"F0.wireOp",EDGE,"E47.MirrorCS"),sQuery(id+"F0.wireOp",EDGE,"E48.MirrorCS"),sQuery(id+"F0.wireOp",EDGE,"E49.MirrorCS"),sQuery(id+"F0.wireOp",EDGE,"E50.MirrorCS"),sQuery(id+"F0.wireOp",EDGE,"E51")])],"isStart":true}),makeQuery(id+"F1.opExtrude","SWEPT_FACE",FACE,{"disambiguationData":[OSD([subQ3,subQ0])]}),makeQuery(id+"F1.opExtrude","SWEPT_FACE",FACE,{"disambiguationData":[OSD([subQ2,subQ1])]}),makeQuery(id+"F3.opExtrude","SWEPT_FACE",FACE,{"disambiguationData":[OSD([sQuery(id+"F2.wireOp",EDGE,"E65.MirrorCS")])]})])],"derivedFrom":makeQuery(id+"F1.opExtrude","CAP_EDGE",EDGE,{"disambiguationData":[OSD([subQ2,subQ1])],"isStart":true})});}
            fillet(context, id + "F4", {"entities" : qUnion([Q0, Q1, Q2, Q3, Q4, Q5, Q6, Q7, Q8, Q9, Q10, Q11, Q12, Q13, Q14, Q15, Q16, Q17]), "radius" : 1.27 * mm, "tangentPropagation" : true, "allowEdgeOverflow" : false});
        }
        {
            var Q0;
            {var subQ0=sQuery(id+"F0.wireOp",EDGE,"E39.MirrorCS");var subQ1=sQuery(id+"F0.wireOp",EDGE,"E31.MirrorCS");Q0=makeQuery(id+"F3.boolean.opBoolean","SPLIT",EDGE,{"disambiguationData":[TD([makeQuery(id+"F1.opExtrude","CAP_FACE",FACE,{"disambiguationData":[OSD([sQuery(id+"F0.wireOp",EDGE,"E15"),sQuery(id+"F0.wireOp",EDGE,"E16"),sQuery(id+"F0.wireOp",EDGE,"E17"),sQuery(id+"F0.wireOp",EDGE,"E20"),sQuery(id+"F0.wireOp",EDGE,"E27.MirrorCS"),sQuery(id+"F0.wireOp",EDGE,"E29.MirrorCS"),sQuery(id+"F0.wireOp",EDGE,"E30.MirrorCS"),sQuery(id+"F0.wireOp",EDGE,"E28.MirrorCS"),sQuery(id+"F0.wireOp",EDGE,"E33.MirrorCS"),sQuery(id+"F0.wireOp",EDGE,"E34.MirrorCS"),subQ1,sQuery(id+"F0.wireOp",EDGE,"E36.MirrorCS"),sQuery(id+"F0.wireOp",EDGE,"E38.MirrorCS"),subQ0,sQuery(id+"F0.wireOp",EDGE,"E42.MirrorCS"),sQuery(id+"F0.wireOp",EDGE,"E43.MirrorCS"),sQuery(id+"F0.wireOp",EDGE,"E46"),sQuery(id+"F0.wireOp",EDGE,"E47.MirrorCS"),sQuery(id+"F0.wireOp",EDGE,"E48.MirrorCS"),sQuery(id+"F0.wireOp",EDGE,"E49.MirrorCS"),sQuery(id+"F0.wireOp",EDGE,"E50.MirrorCS"),sQuery(id+"F0.wireOp",EDGE,"E51")])],"isStart":true}),makeQuery(id+"F1.opExtrude","SWEPT_FACE",FACE,{"disambiguationData":[OSD([subQ1,subQ0])]}),makeQuery(id+"F3.opExtrude","SWEPT_FACE",FACE,{"disambiguationData":[OSD([sQuery(id+"F2.wireOp",EDGE,"E65.MirrorCS")])]}),makeQuery(id+"F3.opExtrude","SWEPT_FACE",FACE,{"disambiguationData":[OSD([sQuery(id+"F2.wireOp",EDGE,"E67.MirrorCS")])]})])],"derivedFrom":makeQuery(id+"F1.opExtrude","CAP_EDGE",EDGE,{"disambiguationData":[OSD([subQ1,subQ0])],"isStart":true})});}
            var Q1;
            {var subQ0=sQuery(id+"F0.wireOp",EDGE,"E39.MirrorCS");var subQ1=sQuery(id+"F0.wireOp",EDGE,"E31.MirrorCS");Q1=makeQuery(id+"F3.boolean.opBoolean","SPLIT",EDGE,{"disambiguationData":[TD([makeQuery(id+"F1.opExtrude","CAP_FACE",FACE,{"disambiguationData":[OSD([sQuery(id+"F0.wireOp",EDGE,"E15"),sQuery(id+"F0.wireOp",EDGE,"E16"),sQuery(id+"F0.wireOp",EDGE,"E17"),sQuery(id+"F0.wireOp",EDGE,"E20"),sQuery(id+"F0.wireOp",EDGE,"E27.MirrorCS"),sQuery(id+"F0.wireOp",EDGE,"E29.MirrorCS"),sQuery(id+"F0.wireOp",EDGE,"E30.MirrorCS"),sQuery(id+"F0.wireOp",EDGE,"E28.MirrorCS"),sQuery(id+"F0.wireOp",EDGE,"E33.MirrorCS"),sQuery(id+"F0.wireOp",EDGE,"E34.MirrorCS"),subQ1,sQuery(id+"F0.wireOp",EDGE,"E36.MirrorCS"),sQuery(id+"F0.wireOp",EDGE,"E38.MirrorCS"),subQ0,sQuery(id+"F0.wireOp",EDGE,"E42.MirrorCS"),sQuery(id+"F0.wireOp",EDGE,"E43.MirrorCS"),sQuery(id+"F0.wireOp",EDGE,"E46"),sQuery(id+"F0.wireOp",EDGE,"E47.MirrorCS"),sQuery(id+"F0.wireOp",EDGE,"E48.MirrorCS"),sQuery(id+"F0.wireOp",EDGE,"E49.MirrorCS"),sQuery(id+"F0.wireOp",EDGE,"E50.MirrorCS"),sQuery(id+"F0.wireOp",EDGE,"E51")])],"isStart":true}),makeQuery(id+"F1.opExtrude","SWEPT_FACE",FACE,{"disambiguationData":[OSD([subQ1,subQ0])]}),makeQuery(id+"F3.opExtrude","SWEPT_FACE",FACE,{"disambiguationData":[OSD([sQuery(id+"F2.wireOp",EDGE,"E67.MirrorCS")])]}),makeQuery(id+"F3.opExtrude","SWEPT_FACE",FACE,{"disambiguationData":[OSD([sQuery(id+"F2.wireOp",EDGE,"E69.MirrorCS")])]})])],"derivedFrom":makeQuery(id+"F1.opExtrude","CAP_EDGE",EDGE,{"disambiguationData":[OSD([subQ1,subQ0])],"isStart":true})});}
            var Q2;
            {var subQ0=sQuery(id+"F0.wireOp",EDGE,"E39.MirrorCS");var subQ1=sQuery(id+"F0.wireOp",EDGE,"E31.MirrorCS");Q2=makeQuery(id+"F3.boolean.opBoolean","SPLIT",EDGE,{"disambiguationData":[TD([makeQuery(id+"F1.opExtrude","CAP_FACE",FACE,{"disambiguationData":[OSD([sQuery(id+"F0.wireOp",EDGE,"E15"),sQuery(id+"F0.wireOp",EDGE,"E16"),sQuery(id+"F0.wireOp",EDGE,"E17"),sQuery(id+"F0.wireOp",EDGE,"E20"),sQuery(id+"F0.wireOp",EDGE,"E27.MirrorCS"),sQuery(id+"F0.wireOp",EDGE,"E29.MirrorCS"),sQuery(id+"F0.wireOp",EDGE,"E30.MirrorCS"),sQuery(id+"F0.wireOp",EDGE,"E28.MirrorCS"),sQuery(id+"F0.wireOp",EDGE,"E33.MirrorCS"),sQuery(id+"F0.wireOp",EDGE,"E34.MirrorCS"),subQ1,sQuery(id+"F0.wireOp",EDGE,"E36.MirrorCS"),sQuery(id+"F0.wireOp",EDGE,"E38.MirrorCS"),subQ0,sQuery(id+"F0.wireOp",EDGE,"E42.MirrorCS"),sQuery(id+"F0.wireOp",EDGE,"E43.MirrorCS"),sQuery(id+"F0.wireOp",EDGE,"E46"),sQuery(id+"F0.wireOp",EDGE,"E47.MirrorCS"),sQuery(id+"F0.wireOp",EDGE,"E48.MirrorCS"),sQuery(id+"F0.wireOp",EDGE,"E49.MirrorCS"),sQuery(id+"F0.wireOp",EDGE,"E50.MirrorCS"),sQuery(id+"F0.wireOp",EDGE,"E51")])],"isStart":true}),makeQuery(id+"F1.opExtrude","SWEPT_FACE",FACE,{"disambiguationData":[OSD([subQ1,subQ0])]}),makeQuery(id+"F3.opExtrude","SWEPT_FACE",FACE,{"disambiguationData":[OSD([sQuery(id+"F2.wireOp",EDGE,"E69.MirrorCS")])]}),makeQuery(id+"F3.opExtrude","SWEPT_FACE",FACE,{"disambiguationData":[OSD([sQuery(id+"F2.wireOp",EDGE,"E70.MirrorCS")])]})])],"derivedFrom":makeQuery(id+"F1.opExtrude","CAP_EDGE",EDGE,{"disambiguationData":[OSD([subQ1,subQ0])],"isStart":true})});}
            var Q3;
            {var subQ0=sQuery(id+"F0.wireOp",EDGE,"E39.MirrorCS");var subQ1=sQuery(id+"F0.wireOp",EDGE,"E31.MirrorCS");Q3=makeQuery(id+"F3.boolean.opBoolean","SPLIT",EDGE,{"disambiguationData":[TD([makeQuery(id+"F1.opExtrude","CAP_FACE",FACE,{"disambiguationData":[OSD([sQuery(id+"F0.wireOp",EDGE,"E15"),sQuery(id+"F0.wireOp",EDGE,"E16"),sQuery(id+"F0.wireOp",EDGE,"E17"),sQuery(id+"F0.wireOp",EDGE,"E20"),sQuery(id+"F0.wireOp",EDGE,"E27.MirrorCS"),sQuery(id+"F0.wireOp",EDGE,"E29.MirrorCS"),sQuery(id+"F0.wireOp",EDGE,"E30.MirrorCS"),sQuery(id+"F0.wireOp",EDGE,"E28.MirrorCS"),sQuery(id+"F0.wireOp",EDGE,"E33.MirrorCS"),sQuery(id+"F0.wireOp",EDGE,"E34.MirrorCS"),subQ1,sQuery(id+"F0.wireOp",EDGE,"E36.MirrorCS"),sQuery(id+"F0.wireOp",EDGE,"E38.MirrorCS"),subQ0,sQuery(id+"F0.wireOp",EDGE,"E42.MirrorCS"),sQuery(id+"F0.wireOp",EDGE,"E43.MirrorCS"),sQuery(id+"F0.wireOp",EDGE,"E46"),sQuery(id+"F0.wireOp",EDGE,"E47.MirrorCS"),sQuery(id+"F0.wireOp",EDGE,"E48.MirrorCS"),sQuery(id+"F0.wireOp",EDGE,"E49.MirrorCS"),sQuery(id+"F0.wireOp",EDGE,"E50.MirrorCS"),sQuery(id+"F0.wireOp",EDGE,"E51")])],"isStart":true}),makeQuery(id+"F1.opExtrude","SWEPT_FACE",FACE,{"disambiguationData":[OSD([subQ1,subQ0])]}),makeQuery(id+"F3.opExtrude","SWEPT_FACE",FACE,{"disambiguationData":[OSD([sQuery(id+"F2.wireOp",EDGE,"E70.MirrorCS")])]}),makeQuery(id+"F3.opExtrude","SWEPT_FACE",FACE,{"disambiguationData":[OSD([sQuery(id+"F2.wireOp",EDGE,"E71.MirrorCS")])]})])],"derivedFrom":makeQuery(id+"F1.opExtrude","CAP_EDGE",EDGE,{"disambiguationData":[OSD([subQ1,subQ0])],"isStart":true})});}
            var Q4;
            {var subQ0=sQuery(id+"F0.wireOp",EDGE,"E39.MirrorCS");var subQ1=sQuery(id+"F0.wireOp",EDGE,"E31.MirrorCS");Q4=makeQuery(id+"F3.boolean.opBoolean","SPLIT",EDGE,{"disambiguationData":[TD([makeQuery(id+"F1.opExtrude","CAP_FACE",FACE,{"disambiguationData":[OSD([sQuery(id+"F0.wireOp",EDGE,"E15"),sQuery(id+"F0.wireOp",EDGE,"E16"),sQuery(id+"F0.wireOp",EDGE,"E17"),sQuery(id+"F0.wireOp",EDGE,"E20"),sQuery(id+"F0.wireOp",EDGE,"E27.MirrorCS"),sQuery(id+"F0.wireOp",EDGE,"E29.MirrorCS"),sQuery(id+"F0.wireOp",EDGE,"E30.MirrorCS"),sQuery(id+"F0.wireOp",EDGE,"E28.MirrorCS"),sQuery(id+"F0.wireOp",EDGE,"E33.MirrorCS"),sQuery(id+"F0.wireOp",EDGE,"E34.MirrorCS"),subQ1,sQuery(id+"F0.wireOp",EDGE,"E36.MirrorCS"),sQuery(id+"F0.wireOp",EDGE,"E38.MirrorCS"),subQ0,sQuery(id+"F0.wireOp",EDGE,"E42.MirrorCS"),sQuery(id+"F0.wireOp",EDGE,"E43.MirrorCS"),sQuery(id+"F0.wireOp",EDGE,"E46"),sQuery(id+"F0.wireOp",EDGE,"E47.MirrorCS"),sQuery(id+"F0.wireOp",EDGE,"E48.MirrorCS"),sQuery(id+"F0.wireOp",EDGE,"E49.MirrorCS"),sQuery(id+"F0.wireOp",EDGE,"E50.MirrorCS"),sQuery(id+"F0.wireOp",EDGE,"E51")])],"isStart":true}),makeQuery(id+"F1.opExtrude","SWEPT_FACE",FACE,{"disambiguationData":[OSD([subQ1,subQ0])]}),makeQuery(id+"F3.opExtrude","SWEPT_FACE",FACE,{"disambiguationData":[OSD([sQuery(id+"F2.wireOp",EDGE,"E71.MirrorCS")])]}),makeQuery(id+"F3.opExtrude","SWEPT_FACE",FACE,{"disambiguationData":[OSD([sQuery(id+"F2.wireOp",EDGE,"E72.MirrorCS")])]})])],"derivedFrom":makeQuery(id+"F1.opExtrude","CAP_EDGE",EDGE,{"disambiguationData":[OSD([subQ1,subQ0])],"isStart":true})});}
            var Q5;
            {var subQ0=sQuery(id+"F0.wireOp",EDGE,"E39.MirrorCS");var subQ1=sQuery(id+"F0.wireOp",EDGE,"E31.MirrorCS");Q5=makeQuery(id+"F3.boolean.opBoolean","SPLIT",EDGE,{"disambiguationData":[TD([makeQuery(id+"F1.opExtrude","CAP_FACE",FACE,{"disambiguationData":[OSD([sQuery(id+"F0.wireOp",EDGE,"E15"),sQuery(id+"F0.wireOp",EDGE,"E16"),sQuery(id+"F0.wireOp",EDGE,"E17"),sQuery(id+"F0.wireOp",EDGE,"E20"),sQuery(id+"F0.wireOp",EDGE,"E27.MirrorCS"),sQuery(id+"F0.wireOp",EDGE,"E29.MirrorCS"),sQuery(id+"F0.wireOp",EDGE,"E30.MirrorCS"),sQuery(id+"F0.wireOp",EDGE,"E28.MirrorCS"),sQuery(id+"F0.wireOp",EDGE,"E33.MirrorCS"),sQuery(id+"F0.wireOp",EDGE,"E34.MirrorCS"),subQ1,sQuery(id+"F0.wireOp",EDGE,"E36.MirrorCS"),sQuery(id+"F0.wireOp",EDGE,"E38.MirrorCS"),subQ0,sQuery(id+"F0.wireOp",EDGE,"E42.MirrorCS"),sQuery(id+"F0.wireOp",EDGE,"E43.MirrorCS"),sQuery(id+"F0.wireOp",EDGE,"E46"),sQuery(id+"F0.wireOp",EDGE,"E47.MirrorCS"),sQuery(id+"F0.wireOp",EDGE,"E48.MirrorCS"),sQuery(id+"F0.wireOp",EDGE,"E49.MirrorCS"),sQuery(id+"F0.wireOp",EDGE,"E50.MirrorCS"),sQuery(id+"F0.wireOp",EDGE,"E51")])],"isStart":false}),makeQuery(id+"F1.opExtrude","SWEPT_FACE",FACE,{"disambiguationData":[OSD([subQ1,subQ0])]}),makeQuery(id+"F3.opExtrude","SWEPT_FACE",FACE,{"disambiguationData":[OSD([sQuery(id+"F2.wireOp",EDGE,"E71.MirrorCS")])]}),makeQuery(id+"F3.opExtrude","SWEPT_FACE",FACE,{"disambiguationData":[OSD([sQuery(id+"F2.wireOp",EDGE,"E72.MirrorCS")])]})])],"derivedFrom":makeQuery(id+"F1.opExtrude","CAP_EDGE",EDGE,{"disambiguationData":[OSD([subQ1,subQ0])],"isStart":false})});}
            var Q6;
            {var subQ0=sQuery(id+"F0.wireOp",EDGE,"E39.MirrorCS");var subQ1=sQuery(id+"F0.wireOp",EDGE,"E31.MirrorCS");Q6=makeQuery(id+"F3.boolean.opBoolean","SPLIT",EDGE,{"disambiguationData":[TD([makeQuery(id+"F1.opExtrude","CAP_FACE",FACE,{"disambiguationData":[OSD([sQuery(id+"F0.wireOp",EDGE,"E15"),sQuery(id+"F0.wireOp",EDGE,"E16"),sQuery(id+"F0.wireOp",EDGE,"E17"),sQuery(id+"F0.wireOp",EDGE,"E20"),sQuery(id+"F0.wireOp",EDGE,"E27.MirrorCS"),sQuery(id+"F0.wireOp",EDGE,"E29.MirrorCS"),sQuery(id+"F0.wireOp",EDGE,"E30.MirrorCS"),sQuery(id+"F0.wireOp",EDGE,"E28.MirrorCS"),sQuery(id+"F0.wireOp",EDGE,"E33.MirrorCS"),sQuery(id+"F0.wireOp",EDGE,"E34.MirrorCS"),subQ1,sQuery(id+"F0.wireOp",EDGE,"E36.MirrorCS"),sQuery(id+"F0.wireOp",EDGE,"E38.MirrorCS"),subQ0,sQuery(id+"F0.wireOp",EDGE,"E42.MirrorCS"),sQuery(id+"F0.wireOp",EDGE,"E43.MirrorCS"),sQuery(id+"F0.wireOp",EDGE,"E46"),sQuery(id+"F0.wireOp",EDGE,"E47.MirrorCS"),sQuery(id+"F0.wireOp",EDGE,"E48.MirrorCS"),sQuery(id+"F0.wireOp",EDGE,"E49.MirrorCS"),sQuery(id+"F0.wireOp",EDGE,"E50.MirrorCS"),sQuery(id+"F0.wireOp",EDGE,"E51")])],"isStart":false}),makeQuery(id+"F1.opExtrude","SWEPT_FACE",FACE,{"disambiguationData":[OSD([subQ1,subQ0])]}),makeQuery(id+"F3.opExtrude","SWEPT_FACE",FACE,{"disambiguationData":[OSD([sQuery(id+"F2.wireOp",EDGE,"E70.MirrorCS")])]}),makeQuery(id+"F3.opExtrude","SWEPT_FACE",FACE,{"disambiguationData":[OSD([sQuery(id+"F2.wireOp",EDGE,"E71.MirrorCS")])]})])],"derivedFrom":makeQuery(id+"F1.opExtrude","CAP_EDGE",EDGE,{"disambiguationData":[OSD([subQ1,subQ0])],"isStart":false})});}
            var Q7;
            {var subQ0=sQuery(id+"F0.wireOp",EDGE,"E39.MirrorCS");var subQ1=sQuery(id+"F0.wireOp",EDGE,"E31.MirrorCS");Q7=makeQuery(id+"F3.boolean.opBoolean","SPLIT",EDGE,{"disambiguationData":[TD([makeQuery(id+"F1.opExtrude","CAP_FACE",FACE,{"disambiguationData":[OSD([sQuery(id+"F0.wireOp",EDGE,"E15"),sQuery(id+"F0.wireOp",EDGE,"E16"),sQuery(id+"F0.wireOp",EDGE,"E17"),sQuery(id+"F0.wireOp",EDGE,"E20"),sQuery(id+"F0.wireOp",EDGE,"E27.MirrorCS"),sQuery(id+"F0.wireOp",EDGE,"E29.MirrorCS"),sQuery(id+"F0.wireOp",EDGE,"E30.MirrorCS"),sQuery(id+"F0.wireOp",EDGE,"E28.MirrorCS"),sQuery(id+"F0.wireOp",EDGE,"E33.MirrorCS"),sQuery(id+"F0.wireOp",EDGE,"E34.MirrorCS"),subQ1,sQuery(id+"F0.wireOp",EDGE,"E36.MirrorCS"),sQuery(id+"F0.wireOp",EDGE,"E38.MirrorCS"),subQ0,sQuery(id+"F0.wireOp",EDGE,"E42.MirrorCS"),sQuery(id+"F0.wireOp",EDGE,"E43.MirrorCS"),sQuery(id+"F0.wireOp",EDGE,"E46"),sQuery(id+"F0.wireOp",EDGE,"E47.MirrorCS"),sQuery(id+"F0.wireOp",EDGE,"E48.MirrorCS"),sQuery(id+"F0.wireOp",EDGE,"E49.MirrorCS"),sQuery(id+"F0.wireOp",EDGE,"E50.MirrorCS"),sQuery(id+"F0.wireOp",EDGE,"E51")])],"isStart":false}),makeQuery(id+"F1.opExtrude","SWEPT_FACE",FACE,{"disambiguationData":[OSD([subQ1,subQ0])]}),makeQuery(id+"F3.opExtrude","SWEPT_FACE",FACE,{"disambiguationData":[OSD([sQuery(id+"F2.wireOp",EDGE,"E69.MirrorCS")])]}),makeQuery(id+"F3.opExtrude","SWEPT_FACE",FACE,{"disambiguationData":[OSD([sQuery(id+"F2.wireOp",EDGE,"E70.MirrorCS")])]})])],"derivedFrom":makeQuery(id+"F1.opExtrude","CAP_EDGE",EDGE,{"disambiguationData":[OSD([subQ1,subQ0])],"isStart":false})});}
            var Q8;
            {var subQ0=sQuery(id+"F0.wireOp",EDGE,"E39.MirrorCS");var subQ1=sQuery(id+"F0.wireOp",EDGE,"E31.MirrorCS");Q8=makeQuery(id+"F3.boolean.opBoolean","SPLIT",EDGE,{"disambiguationData":[TD([makeQuery(id+"F1.opExtrude","CAP_FACE",FACE,{"disambiguationData":[OSD([sQuery(id+"F0.wireOp",EDGE,"E15"),sQuery(id+"F0.wireOp",EDGE,"E16"),sQuery(id+"F0.wireOp",EDGE,"E17"),sQuery(id+"F0.wireOp",EDGE,"E20"),sQuery(id+"F0.wireOp",EDGE,"E27.MirrorCS"),sQuery(id+"F0.wireOp",EDGE,"E29.MirrorCS"),sQuery(id+"F0.wireOp",EDGE,"E30.MirrorCS"),sQuery(id+"F0.wireOp",EDGE,"E28.MirrorCS"),sQuery(id+"F0.wireOp",EDGE,"E33.MirrorCS"),sQuery(id+"F0.wireOp",EDGE,"E34.MirrorCS"),subQ1,sQuery(id+"F0.wireOp",EDGE,"E36.MirrorCS"),sQuery(id+"F0.wireOp",EDGE,"E38.MirrorCS"),subQ0,sQuery(id+"F0.wireOp",EDGE,"E42.MirrorCS"),sQuery(id+"F0.wireOp",EDGE,"E43.MirrorCS"),sQuery(id+"F0.wireOp",EDGE,"E46"),sQuery(id+"F0.wireOp",EDGE,"E47.MirrorCS"),sQuery(id+"F0.wireOp",EDGE,"E48.MirrorCS"),sQuery(id+"F0.wireOp",EDGE,"E49.MirrorCS"),sQuery(id+"F0.wireOp",EDGE,"E50.MirrorCS"),sQuery(id+"F0.wireOp",EDGE,"E51")])],"isStart":false}),makeQuery(id+"F1.opExtrude","SWEPT_FACE",FACE,{"disambiguationData":[OSD([subQ1,subQ0])]}),makeQuery(id+"F3.opExtrude","SWEPT_FACE",FACE,{"disambiguationData":[OSD([sQuery(id+"F2.wireOp",EDGE,"E67.MirrorCS")])]}),makeQuery(id+"F3.opExtrude","SWEPT_FACE",FACE,{"disambiguationData":[OSD([sQuery(id+"F2.wireOp",EDGE,"E69.MirrorCS")])]})])],"derivedFrom":makeQuery(id+"F1.opExtrude","CAP_EDGE",EDGE,{"disambiguationData":[OSD([subQ1,subQ0])],"isStart":false})});}
            var Q9;
            {var subQ0=sQuery(id+"F0.wireOp",EDGE,"E39.MirrorCS");var subQ1=sQuery(id+"F0.wireOp",EDGE,"E31.MirrorCS");Q9=makeQuery(id+"F3.boolean.opBoolean","SPLIT",EDGE,{"disambiguationData":[TD([makeQuery(id+"F1.opExtrude","CAP_FACE",FACE,{"disambiguationData":[OSD([sQuery(id+"F0.wireOp",EDGE,"E15"),sQuery(id+"F0.wireOp",EDGE,"E16"),sQuery(id+"F0.wireOp",EDGE,"E17"),sQuery(id+"F0.wireOp",EDGE,"E20"),sQuery(id+"F0.wireOp",EDGE,"E27.MirrorCS"),sQuery(id+"F0.wireOp",EDGE,"E29.MirrorCS"),sQuery(id+"F0.wireOp",EDGE,"E30.MirrorCS"),sQuery(id+"F0.wireOp",EDGE,"E28.MirrorCS"),sQuery(id+"F0.wireOp",EDGE,"E33.MirrorCS"),sQuery(id+"F0.wireOp",EDGE,"E34.MirrorCS"),subQ1,sQuery(id+"F0.wireOp",EDGE,"E36.MirrorCS"),sQuery(id+"F0.wireOp",EDGE,"E38.MirrorCS"),subQ0,sQuery(id+"F0.wireOp",EDGE,"E42.MirrorCS"),sQuery(id+"F0.wireOp",EDGE,"E43.MirrorCS"),sQuery(id+"F0.wireOp",EDGE,"E46"),sQuery(id+"F0.wireOp",EDGE,"E47.MirrorCS"),sQuery(id+"F0.wireOp",EDGE,"E48.MirrorCS"),sQuery(id+"F0.wireOp",EDGE,"E49.MirrorCS"),sQuery(id+"F0.wireOp",EDGE,"E50.MirrorCS"),sQuery(id+"F0.wireOp",EDGE,"E51")])],"isStart":false}),makeQuery(id+"F1.opExtrude","SWEPT_FACE",FACE,{"disambiguationData":[OSD([subQ1,subQ0])]}),makeQuery(id+"F3.opExtrude","SWEPT_FACE",FACE,{"disambiguationData":[OSD([sQuery(id+"F2.wireOp",EDGE,"E65.MirrorCS")])]}),makeQuery(id+"F3.opExtrude","SWEPT_FACE",FACE,{"disambiguationData":[OSD([sQuery(id+"F2.wireOp",EDGE,"E67.MirrorCS")])]})])],"derivedFrom":makeQuery(id+"F1.opExtrude","CAP_EDGE",EDGE,{"disambiguationData":[OSD([subQ1,subQ0])],"isStart":false})});}
            var Q10;
            {var subQ0=sQuery(id+"F0.wireOp",EDGE,"E28.MirrorCS");var subQ1=sQuery(id+"F0.wireOp",EDGE,"E20");Q10=makeQuery(id+"F3.boolean.opBoolean","SPLIT",EDGE,{"disambiguationData":[TD([makeQuery(id+"F1.opExtrude","CAP_FACE",FACE,{"disambiguationData":[OSD([sQuery(id+"F0.wireOp",EDGE,"E15"),sQuery(id+"F0.wireOp",EDGE,"E16"),sQuery(id+"F0.wireOp",EDGE,"E17"),subQ1,sQuery(id+"F0.wireOp",EDGE,"E27.MirrorCS"),sQuery(id+"F0.wireOp",EDGE,"E29.MirrorCS"),sQuery(id+"F0.wireOp",EDGE,"E30.MirrorCS"),subQ0,sQuery(id+"F0.wireOp",EDGE,"E33.MirrorCS"),sQuery(id+"F0.wireOp",EDGE,"E34.MirrorCS"),sQuery(id+"F0.wireOp",EDGE,"E31.MirrorCS"),sQuery(id+"F0.wireOp",EDGE,"E36.MirrorCS"),sQuery(id+"F0.wireOp",EDGE,"E38.MirrorCS"),sQuery(id+"F0.wireOp",EDGE,"E39.MirrorCS"),sQuery(id+"F0.wireOp",EDGE,"E42.MirrorCS"),sQuery(id+"F0.wireOp",EDGE,"E43.MirrorCS"),sQuery(id+"F0.wireOp",EDGE,"E46"),sQuery(id+"F0.wireOp",EDGE,"E47.MirrorCS"),sQuery(id+"F0.wireOp",EDGE,"E48.MirrorCS"),sQuery(id+"F0.wireOp",EDGE,"E49.MirrorCS"),sQuery(id+"F0.wireOp",EDGE,"E50.MirrorCS"),sQuery(id+"F0.wireOp",EDGE,"E51")])],"isStart":true}),makeQuery(id+"F1.opExtrude","SWEPT_FACE",FACE,{"disambiguationData":[OSD([subQ1,subQ0])]}),makeQuery(id+"F3.opExtrude","SWEPT_FACE",FACE,{"disambiguationData":[OSD([sQuery(id+"F2.wireOp",EDGE,"E56")])]}),makeQuery(id+"F3.opExtrude","SWEPT_FACE",FACE,{"disambiguationData":[OSD([sQuery(id+"F2.wireOp",EDGE,"E60")])]})])],"derivedFrom":makeQuery(id+"F1.opExtrude","CAP_EDGE",EDGE,{"disambiguationData":[OSD([subQ1,subQ0])],"isStart":true})});}
            var Q11;
            {var subQ0=sQuery(id+"F0.wireOp",EDGE,"E28.MirrorCS");var subQ1=sQuery(id+"F0.wireOp",EDGE,"E20");Q11=makeQuery(id+"F3.boolean.opBoolean","SPLIT",EDGE,{"disambiguationData":[TD([makeQuery(id+"F1.opExtrude","CAP_FACE",FACE,{"disambiguationData":[OSD([sQuery(id+"F0.wireOp",EDGE,"E15"),sQuery(id+"F0.wireOp",EDGE,"E16"),sQuery(id+"F0.wireOp",EDGE,"E17"),subQ1,sQuery(id+"F0.wireOp",EDGE,"E27.MirrorCS"),sQuery(id+"F0.wireOp",EDGE,"E29.MirrorCS"),sQuery(id+"F0.wireOp",EDGE,"E30.MirrorCS"),subQ0,sQuery(id+"F0.wireOp",EDGE,"E33.MirrorCS"),sQuery(id+"F0.wireOp",EDGE,"E34.MirrorCS"),sQuery(id+"F0.wireOp",EDGE,"E31.MirrorCS"),sQuery(id+"F0.wireOp",EDGE,"E36.MirrorCS"),sQuery(id+"F0.wireOp",EDGE,"E38.MirrorCS"),sQuery(id+"F0.wireOp",EDGE,"E39.MirrorCS"),sQuery(id+"F0.wireOp",EDGE,"E42.MirrorCS"),sQuery(id+"F0.wireOp",EDGE,"E43.MirrorCS"),sQuery(id+"F0.wireOp",EDGE,"E46"),sQuery(id+"F0.wireOp",EDGE,"E47.MirrorCS"),sQuery(id+"F0.wireOp",EDGE,"E48.MirrorCS"),sQuery(id+"F0.wireOp",EDGE,"E49.MirrorCS"),sQuery(id+"F0.wireOp",EDGE,"E50.MirrorCS"),sQuery(id+"F0.wireOp",EDGE,"E51")])],"isStart":true}),makeQuery(id+"F1.opExtrude","SWEPT_FACE",FACE,{"disambiguationData":[OSD([subQ1,subQ0])]}),makeQuery(id+"F3.opExtrude","SWEPT_FACE",FACE,{"disambiguationData":[OSD([sQuery(id+"F2.wireOp",EDGE,"E53")])]}),makeQuery(id+"F3.opExtrude","SWEPT_FACE",FACE,{"disambiguationData":[OSD([sQuery(id+"F2.wireOp",EDGE,"E56")])]})])],"derivedFrom":makeQuery(id+"F1.opExtrude","CAP_EDGE",EDGE,{"disambiguationData":[OSD([subQ1,subQ0])],"isStart":true})});}
            var Q12;
            {var subQ0=sQuery(id+"F0.wireOp",EDGE,"E28.MirrorCS");var subQ1=sQuery(id+"F0.wireOp",EDGE,"E20");Q12=makeQuery(id+"F3.boolean.opBoolean","SPLIT",EDGE,{"disambiguationData":[TD([makeQuery(id+"F1.opExtrude","CAP_FACE",FACE,{"disambiguationData":[OSD([sQuery(id+"F0.wireOp",EDGE,"E15"),sQuery(id+"F0.wireOp",EDGE,"E16"),sQuery(id+"F0.wireOp",EDGE,"E17"),subQ1,sQuery(id+"F0.wireOp",EDGE,"E27.MirrorCS"),sQuery(id+"F0.wireOp",EDGE,"E29.MirrorCS"),sQuery(id+"F0.wireOp",EDGE,"E30.MirrorCS"),subQ0,sQuery(id+"F0.wireOp",EDGE,"E33.MirrorCS"),sQuery(id+"F0.wireOp",EDGE,"E34.MirrorCS"),sQuery(id+"F0.wireOp",EDGE,"E31.MirrorCS"),sQuery(id+"F0.wireOp",EDGE,"E36.MirrorCS"),sQuery(id+"F0.wireOp",EDGE,"E38.MirrorCS"),sQuery(id+"F0.wireOp",EDGE,"E39.MirrorCS"),sQuery(id+"F0.wireOp",EDGE,"E42.MirrorCS"),sQuery(id+"F0.wireOp",EDGE,"E43.MirrorCS"),sQuery(id+"F0.wireOp",EDGE,"E46"),sQuery(id+"F0.wireOp",EDGE,"E47.MirrorCS"),sQuery(id+"F0.wireOp",EDGE,"E48.MirrorCS"),sQuery(id+"F0.wireOp",EDGE,"E49.MirrorCS"),sQuery(id+"F0.wireOp",EDGE,"E50.MirrorCS"),sQuery(id+"F0.wireOp",EDGE,"E51")])],"isStart":true}),makeQuery(id+"F1.opExtrude","SWEPT_FACE",FACE,{"disambiguationData":[OSD([subQ1,subQ0])]}),makeQuery(id+"F3.opExtrude","SWEPT_FACE",FACE,{"disambiguationData":[OSD([sQuery(id+"F2.wireOp",EDGE,"E52")])]}),makeQuery(id+"F3.opExtrude","SWEPT_FACE",FACE,{"disambiguationData":[OSD([sQuery(id+"F2.wireOp",EDGE,"E53")])]})])],"derivedFrom":makeQuery(id+"F1.opExtrude","CAP_EDGE",EDGE,{"disambiguationData":[OSD([subQ1,subQ0])],"isStart":true})});}
            var Q13;
            {var subQ0=sQuery(id+"F0.wireOp",EDGE,"E28.MirrorCS");var subQ1=sQuery(id+"F0.wireOp",EDGE,"E20");Q13=makeQuery(id+"F3.boolean.opBoolean","SPLIT",EDGE,{"disambiguationData":[TD([makeQuery(id+"F1.opExtrude","CAP_FACE",FACE,{"disambiguationData":[OSD([sQuery(id+"F0.wireOp",EDGE,"E15"),sQuery(id+"F0.wireOp",EDGE,"E16"),sQuery(id+"F0.wireOp",EDGE,"E17"),subQ1,sQuery(id+"F0.wireOp",EDGE,"E27.MirrorCS"),sQuery(id+"F0.wireOp",EDGE,"E29.MirrorCS"),sQuery(id+"F0.wireOp",EDGE,"E30.MirrorCS"),subQ0,sQuery(id+"F0.wireOp",EDGE,"E33.MirrorCS"),sQuery(id+"F0.wireOp",EDGE,"E34.MirrorCS"),sQuery(id+"F0.wireOp",EDGE,"E31.MirrorCS"),sQuery(id+"F0.wireOp",EDGE,"E36.MirrorCS"),sQuery(id+"F0.wireOp",EDGE,"E38.MirrorCS"),sQuery(id+"F0.wireOp",EDGE,"E39.MirrorCS"),sQuery(id+"F0.wireOp",EDGE,"E42.MirrorCS"),sQuery(id+"F0.wireOp",EDGE,"E43.MirrorCS"),sQuery(id+"F0.wireOp",EDGE,"E46"),sQuery(id+"F0.wireOp",EDGE,"E47.MirrorCS"),sQuery(id+"F0.wireOp",EDGE,"E48.MirrorCS"),sQuery(id+"F0.wireOp",EDGE,"E49.MirrorCS"),sQuery(id+"F0.wireOp",EDGE,"E50.MirrorCS"),sQuery(id+"F0.wireOp",EDGE,"E51")])],"isStart":true}),makeQuery(id+"F1.opExtrude","SWEPT_FACE",FACE,{"disambiguationData":[OSD([subQ1,subQ0])]}),makeQuery(id+"F3.opExtrude","SWEPT_FACE",FACE,{"disambiguationData":[OSD([sQuery(id+"F2.wireOp",EDGE,"E52")])]}),makeQuery(id+"F3.opExtrude","SWEPT_FACE",FACE,{"disambiguationData":[OSD([sQuery(id+"F2.wireOp",EDGE,"E57")])]})])],"derivedFrom":makeQuery(id+"F1.opExtrude","CAP_EDGE",EDGE,{"disambiguationData":[OSD([subQ1,subQ0])],"isStart":true})});}
            var Q14;
            {var subQ0=sQuery(id+"F0.wireOp",EDGE,"E28.MirrorCS");var subQ1=sQuery(id+"F0.wireOp",EDGE,"E20");Q14=makeQuery(id+"F3.boolean.opBoolean","SPLIT",EDGE,{"disambiguationData":[TD([makeQuery(id+"F1.opExtrude","CAP_FACE",FACE,{"disambiguationData":[OSD([sQuery(id+"F0.wireOp",EDGE,"E15"),sQuery(id+"F0.wireOp",EDGE,"E16"),sQuery(id+"F0.wireOp",EDGE,"E17"),subQ1,sQuery(id+"F0.wireOp",EDGE,"E27.MirrorCS"),sQuery(id+"F0.wireOp",EDGE,"E29.MirrorCS"),sQuery(id+"F0.wireOp",EDGE,"E30.MirrorCS"),subQ0,sQuery(id+"F0.wireOp",EDGE,"E33.MirrorCS"),sQuery(id+"F0.wireOp",EDGE,"E34.MirrorCS"),sQuery(id+"F0.wireOp",EDGE,"E31.MirrorCS"),sQuery(id+"F0.wireOp",EDGE,"E36.MirrorCS"),sQuery(id+"F0.wireOp",EDGE,"E38.MirrorCS"),sQuery(id+"F0.wireOp",EDGE,"E39.MirrorCS"),sQuery(id+"F0.wireOp",EDGE,"E42.MirrorCS"),sQuery(id+"F0.wireOp",EDGE,"E43.MirrorCS"),sQuery(id+"F0.wireOp",EDGE,"E46"),sQuery(id+"F0.wireOp",EDGE,"E47.MirrorCS"),sQuery(id+"F0.wireOp",EDGE,"E48.MirrorCS"),sQuery(id+"F0.wireOp",EDGE,"E49.MirrorCS"),sQuery(id+"F0.wireOp",EDGE,"E50.MirrorCS"),sQuery(id+"F0.wireOp",EDGE,"E51")])],"isStart":true}),makeQuery(id+"F1.opExtrude","SWEPT_FACE",FACE,{"disambiguationData":[OSD([subQ1,subQ0])]}),makeQuery(id+"F3.opExtrude","SWEPT_FACE",FACE,{"disambiguationData":[OSD([sQuery(id+"F2.wireOp",EDGE,"E57")])]}),makeQuery(id+"F3.opExtrude","SWEPT_FACE",FACE,{"disambiguationData":[OSD([sQuery(id+"F2.wireOp",EDGE,"E61")])]})])],"derivedFrom":makeQuery(id+"F1.opExtrude","CAP_EDGE",EDGE,{"disambiguationData":[OSD([subQ1,subQ0])],"isStart":true})});}
            var Q15;
            {var subQ0=sQuery(id+"F0.wireOp",EDGE,"E28.MirrorCS");var subQ1=sQuery(id+"F0.wireOp",EDGE,"E20");Q15=makeQuery(id+"F3.boolean.opBoolean","SPLIT",EDGE,{"disambiguationData":[TD([makeQuery(id+"F1.opExtrude","CAP_FACE",FACE,{"disambiguationData":[OSD([sQuery(id+"F0.wireOp",EDGE,"E15"),sQuery(id+"F0.wireOp",EDGE,"E16"),sQuery(id+"F0.wireOp",EDGE,"E17"),subQ1,sQuery(id+"F0.wireOp",EDGE,"E27.MirrorCS"),sQuery(id+"F0.wireOp",EDGE,"E29.MirrorCS"),sQuery(id+"F0.wireOp",EDGE,"E30.MirrorCS"),subQ0,sQuery(id+"F0.wireOp",EDGE,"E33.MirrorCS"),sQuery(id+"F0.wireOp",EDGE,"E34.MirrorCS"),sQuery(id+"F0.wireOp",EDGE,"E31.MirrorCS"),sQuery(id+"F0.wireOp",EDGE,"E36.MirrorCS"),sQuery(id+"F0.wireOp",EDGE,"E38.MirrorCS"),sQuery(id+"F0.wireOp",EDGE,"E39.MirrorCS"),sQuery(id+"F0.wireOp",EDGE,"E42.MirrorCS"),sQuery(id+"F0.wireOp",EDGE,"E43.MirrorCS"),sQuery(id+"F0.wireOp",EDGE,"E46"),sQuery(id+"F0.wireOp",EDGE,"E47.MirrorCS"),sQuery(id+"F0.wireOp",EDGE,"E48.MirrorCS"),sQuery(id+"F0.wireOp",EDGE,"E49.MirrorCS"),sQuery(id+"F0.wireOp",EDGE,"E50.MirrorCS"),sQuery(id+"F0.wireOp",EDGE,"E51")])],"isStart":false}),makeQuery(id+"F1.opExtrude","SWEPT_FACE",FACE,{"disambiguationData":[OSD([subQ1,subQ0])]}),makeQuery(id+"F3.opExtrude","SWEPT_FACE",FACE,{"disambiguationData":[OSD([sQuery(id+"F2.wireOp",EDGE,"E57")])]}),makeQuery(id+"F3.opExtrude","SWEPT_FACE",FACE,{"disambiguationData":[OSD([sQuery(id+"F2.wireOp",EDGE,"E61")])]})])],"derivedFrom":makeQuery(id+"F1.opExtrude","CAP_EDGE",EDGE,{"disambiguationData":[OSD([subQ1,subQ0])],"isStart":false})});}
            var Q16;
            {var subQ0=sQuery(id+"F0.wireOp",EDGE,"E28.MirrorCS");var subQ1=sQuery(id+"F0.wireOp",EDGE,"E20");Q16=makeQuery(id+"F3.boolean.opBoolean","SPLIT",EDGE,{"disambiguationData":[TD([makeQuery(id+"F1.opExtrude","CAP_FACE",FACE,{"disambiguationData":[OSD([sQuery(id+"F0.wireOp",EDGE,"E15"),sQuery(id+"F0.wireOp",EDGE,"E16"),sQuery(id+"F0.wireOp",EDGE,"E17"),subQ1,sQuery(id+"F0.wireOp",EDGE,"E27.MirrorCS"),sQuery(id+"F0.wireOp",EDGE,"E29.MirrorCS"),sQuery(id+"F0.wireOp",EDGE,"E30.MirrorCS"),subQ0,sQuery(id+"F0.wireOp",EDGE,"E33.MirrorCS"),sQuery(id+"F0.wireOp",EDGE,"E34.MirrorCS"),sQuery(id+"F0.wireOp",EDGE,"E31.MirrorCS"),sQuery(id+"F0.wireOp",EDGE,"E36.MirrorCS"),sQuery(id+"F0.wireOp",EDGE,"E38.MirrorCS"),sQuery(id+"F0.wireOp",EDGE,"E39.MirrorCS"),sQuery(id+"F0.wireOp",EDGE,"E42.MirrorCS"),sQuery(id+"F0.wireOp",EDGE,"E43.MirrorCS"),sQuery(id+"F0.wireOp",EDGE,"E46"),sQuery(id+"F0.wireOp",EDGE,"E47.MirrorCS"),sQuery(id+"F0.wireOp",EDGE,"E48.MirrorCS"),sQuery(id+"F0.wireOp",EDGE,"E49.MirrorCS"),sQuery(id+"F0.wireOp",EDGE,"E50.MirrorCS"),sQuery(id+"F0.wireOp",EDGE,"E51")])],"isStart":false}),makeQuery(id+"F1.opExtrude","SWEPT_FACE",FACE,{"disambiguationData":[OSD([subQ1,subQ0])]}),makeQuery(id+"F3.opExtrude","SWEPT_FACE",FACE,{"disambiguationData":[OSD([sQuery(id+"F2.wireOp",EDGE,"E52")])]}),makeQuery(id+"F3.opExtrude","SWEPT_FACE",FACE,{"disambiguationData":[OSD([sQuery(id+"F2.wireOp",EDGE,"E57")])]})])],"derivedFrom":makeQuery(id+"F1.opExtrude","CAP_EDGE",EDGE,{"disambiguationData":[OSD([subQ1,subQ0])],"isStart":false})});}
            var Q17;
            {var subQ0=sQuery(id+"F0.wireOp",EDGE,"E28.MirrorCS");var subQ1=sQuery(id+"F0.wireOp",EDGE,"E20");Q17=makeQuery(id+"F3.boolean.opBoolean","SPLIT",EDGE,{"disambiguationData":[TD([makeQuery(id+"F1.opExtrude","CAP_FACE",FACE,{"disambiguationData":[OSD([sQuery(id+"F0.wireOp",EDGE,"E15"),sQuery(id+"F0.wireOp",EDGE,"E16"),sQuery(id+"F0.wireOp",EDGE,"E17"),subQ1,sQuery(id+"F0.wireOp",EDGE,"E27.MirrorCS"),sQuery(id+"F0.wireOp",EDGE,"E29.MirrorCS"),sQuery(id+"F0.wireOp",EDGE,"E30.MirrorCS"),subQ0,sQuery(id+"F0.wireOp",EDGE,"E33.MirrorCS"),sQuery(id+"F0.wireOp",EDGE,"E34.MirrorCS"),sQuery(id+"F0.wireOp",EDGE,"E31.MirrorCS"),sQuery(id+"F0.wireOp",EDGE,"E36.MirrorCS"),sQuery(id+"F0.wireOp",EDGE,"E38.MirrorCS"),sQuery(id+"F0.wireOp",EDGE,"E39.MirrorCS"),sQuery(id+"F0.wireOp",EDGE,"E42.MirrorCS"),sQuery(id+"F0.wireOp",EDGE,"E43.MirrorCS"),sQuery(id+"F0.wireOp",EDGE,"E46"),sQuery(id+"F0.wireOp",EDGE,"E47.MirrorCS"),sQuery(id+"F0.wireOp",EDGE,"E48.MirrorCS"),sQuery(id+"F0.wireOp",EDGE,"E49.MirrorCS"),sQuery(id+"F0.wireOp",EDGE,"E50.MirrorCS"),sQuery(id+"F0.wireOp",EDGE,"E51")])],"isStart":false}),makeQuery(id+"F1.opExtrude","SWEPT_FACE",FACE,{"disambiguationData":[OSD([subQ1,subQ0])]}),makeQuery(id+"F3.opExtrude","SWEPT_FACE",FACE,{"disambiguationData":[OSD([sQuery(id+"F2.wireOp",EDGE,"E52")])]}),makeQuery(id+"F3.opExtrude","SWEPT_FACE",FACE,{"disambiguationData":[OSD([sQuery(id+"F2.wireOp",EDGE,"E53")])]})])],"derivedFrom":makeQuery(id+"F1.opExtrude","CAP_EDGE",EDGE,{"disambiguationData":[OSD([subQ1,subQ0])],"isStart":false})});}
            var Q18;
            {var subQ0=sQuery(id+"F0.wireOp",EDGE,"E28.MirrorCS");var subQ1=sQuery(id+"F0.wireOp",EDGE,"E20");Q18=makeQuery(id+"F3.boolean.opBoolean","SPLIT",EDGE,{"disambiguationData":[TD([makeQuery(id+"F1.opExtrude","CAP_FACE",FACE,{"disambiguationData":[OSD([sQuery(id+"F0.wireOp",EDGE,"E15"),sQuery(id+"F0.wireOp",EDGE,"E16"),sQuery(id+"F0.wireOp",EDGE,"E17"),subQ1,sQuery(id+"F0.wireOp",EDGE,"E27.MirrorCS"),sQuery(id+"F0.wireOp",EDGE,"E29.MirrorCS"),sQuery(id+"F0.wireOp",EDGE,"E30.MirrorCS"),subQ0,sQuery(id+"F0.wireOp",EDGE,"E33.MirrorCS"),sQuery(id+"F0.wireOp",EDGE,"E34.MirrorCS"),sQuery(id+"F0.wireOp",EDGE,"E31.MirrorCS"),sQuery(id+"F0.wireOp",EDGE,"E36.MirrorCS"),sQuery(id+"F0.wireOp",EDGE,"E38.MirrorCS"),sQuery(id+"F0.wireOp",EDGE,"E39.MirrorCS"),sQuery(id+"F0.wireOp",EDGE,"E42.MirrorCS"),sQuery(id+"F0.wireOp",EDGE,"E43.MirrorCS"),sQuery(id+"F0.wireOp",EDGE,"E46"),sQuery(id+"F0.wireOp",EDGE,"E47.MirrorCS"),sQuery(id+"F0.wireOp",EDGE,"E48.MirrorCS"),sQuery(id+"F0.wireOp",EDGE,"E49.MirrorCS"),sQuery(id+"F0.wireOp",EDGE,"E50.MirrorCS"),sQuery(id+"F0.wireOp",EDGE,"E51")])],"isStart":false}),makeQuery(id+"F1.opExtrude","SWEPT_FACE",FACE,{"disambiguationData":[OSD([subQ1,subQ0])]}),makeQuery(id+"F3.opExtrude","SWEPT_FACE",FACE,{"disambiguationData":[OSD([sQuery(id+"F2.wireOp",EDGE,"E53")])]}),makeQuery(id+"F3.opExtrude","SWEPT_FACE",FACE,{"disambiguationData":[OSD([sQuery(id+"F2.wireOp",EDGE,"E56")])]})])],"derivedFrom":makeQuery(id+"F1.opExtrude","CAP_EDGE",EDGE,{"disambiguationData":[OSD([subQ1,subQ0])],"isStart":false})});}
            var Q19;
            {var subQ0=sQuery(id+"F0.wireOp",EDGE,"E28.MirrorCS");var subQ1=sQuery(id+"F0.wireOp",EDGE,"E20");Q19=makeQuery(id+"F3.boolean.opBoolean","SPLIT",EDGE,{"disambiguationData":[TD([makeQuery(id+"F1.opExtrude","CAP_FACE",FACE,{"disambiguationData":[OSD([sQuery(id+"F0.wireOp",EDGE,"E15"),sQuery(id+"F0.wireOp",EDGE,"E16"),sQuery(id+"F0.wireOp",EDGE,"E17"),subQ1,sQuery(id+"F0.wireOp",EDGE,"E27.MirrorCS"),sQuery(id+"F0.wireOp",EDGE,"E29.MirrorCS"),sQuery(id+"F0.wireOp",EDGE,"E30.MirrorCS"),subQ0,sQuery(id+"F0.wireOp",EDGE,"E33.MirrorCS"),sQuery(id+"F0.wireOp",EDGE,"E34.MirrorCS"),sQuery(id+"F0.wireOp",EDGE,"E31.MirrorCS"),sQuery(id+"F0.wireOp",EDGE,"E36.MirrorCS"),sQuery(id+"F0.wireOp",EDGE,"E38.MirrorCS"),sQuery(id+"F0.wireOp",EDGE,"E39.MirrorCS"),sQuery(id+"F0.wireOp",EDGE,"E42.MirrorCS"),sQuery(id+"F0.wireOp",EDGE,"E43.MirrorCS"),sQuery(id+"F0.wireOp",EDGE,"E46"),sQuery(id+"F0.wireOp",EDGE,"E47.MirrorCS"),sQuery(id+"F0.wireOp",EDGE,"E48.MirrorCS"),sQuery(id+"F0.wireOp",EDGE,"E49.MirrorCS"),sQuery(id+"F0.wireOp",EDGE,"E50.MirrorCS"),sQuery(id+"F0.wireOp",EDGE,"E51")])],"isStart":false}),makeQuery(id+"F1.opExtrude","SWEPT_FACE",FACE,{"disambiguationData":[OSD([subQ1,subQ0])]}),makeQuery(id+"F3.opExtrude","SWEPT_FACE",FACE,{"disambiguationData":[OSD([sQuery(id+"F2.wireOp",EDGE,"E56")])]}),makeQuery(id+"F3.opExtrude","SWEPT_FACE",FACE,{"disambiguationData":[OSD([sQuery(id+"F2.wireOp",EDGE,"E60")])]})])],"derivedFrom":makeQuery(id+"F1.opExtrude","CAP_EDGE",EDGE,{"disambiguationData":[OSD([subQ1,subQ0])],"isStart":false})});}
            var Q20;
            {var subQ0=sQuery(id+"F0.wireOp",EDGE,"E50.MirrorCS");var subQ1=sQuery(id+"F0.wireOp",EDGE,"E48.MirrorCS");Q20=makeQuery(id+"F3.boolean.opBoolean","SPLIT",EDGE,{"disambiguationData":[TD([makeQuery(id+"F1.opExtrude","CAP_FACE",FACE,{"disambiguationData":[OSD([sQuery(id+"F0.wireOp",EDGE,"E15"),sQuery(id+"F0.wireOp",EDGE,"E16"),sQuery(id+"F0.wireOp",EDGE,"E17"),sQuery(id+"F0.wireOp",EDGE,"E20"),sQuery(id+"F0.wireOp",EDGE,"E27.MirrorCS"),sQuery(id+"F0.wireOp",EDGE,"E29.MirrorCS"),sQuery(id+"F0.wireOp",EDGE,"E30.MirrorCS"),sQuery(id+"F0.wireOp",EDGE,"E28.MirrorCS"),sQuery(id+"F0.wireOp",EDGE,"E33.MirrorCS"),sQuery(id+"F0.wireOp",EDGE,"E34.MirrorCS"),sQuery(id+"F0.wireOp",EDGE,"E31.MirrorCS"),sQuery(id+"F0.wireOp",EDGE,"E36.MirrorCS"),sQuery(id+"F0.wireOp",EDGE,"E38.MirrorCS"),sQuery(id+"F0.wireOp",EDGE,"E39.MirrorCS"),sQuery(id+"F0.wireOp",EDGE,"E42.MirrorCS"),sQuery(id+"F0.wireOp",EDGE,"E43.MirrorCS"),sQuery(id+"F0.wireOp",EDGE,"E46"),sQuery(id+"F0.wireOp",EDGE,"E47.MirrorCS"),subQ1,sQuery(id+"F0.wireOp",EDGE,"E49.MirrorCS"),subQ0,sQuery(id+"F0.wireOp",EDGE,"E51")])],"isStart":false}),makeQuery(id+"F1.opExtrude","SWEPT_FACE",FACE,{"disambiguationData":[OSD([subQ1,subQ0])]}),makeQuery(id+"F3.opExtrude","SWEPT_FACE",FACE,{"disambiguationData":[OSD([sQuery(id+"F2.wireOp",EDGE,"E81")])]}),makeQuery(id+"F3.opExtrude","SWEPT_FACE",FACE,{"disambiguationData":[OSD([sQuery(id+"F2.wireOp",EDGE,"E82")])]})])],"derivedFrom":makeQuery(id+"F1.opExtrude","CAP_EDGE",EDGE,{"disambiguationData":[OSD([subQ1,subQ0])],"isStart":false})});}
            var Q21;
            {var subQ0=sQuery(id+"F0.wireOp",EDGE,"E50.MirrorCS");var subQ1=sQuery(id+"F0.wireOp",EDGE,"E48.MirrorCS");Q21=makeQuery(id+"F3.boolean.opBoolean","SPLIT",EDGE,{"disambiguationData":[TD([makeQuery(id+"F1.opExtrude","CAP_FACE",FACE,{"disambiguationData":[OSD([sQuery(id+"F0.wireOp",EDGE,"E15"),sQuery(id+"F0.wireOp",EDGE,"E16"),sQuery(id+"F0.wireOp",EDGE,"E17"),sQuery(id+"F0.wireOp",EDGE,"E20"),sQuery(id+"F0.wireOp",EDGE,"E27.MirrorCS"),sQuery(id+"F0.wireOp",EDGE,"E29.MirrorCS"),sQuery(id+"F0.wireOp",EDGE,"E30.MirrorCS"),sQuery(id+"F0.wireOp",EDGE,"E28.MirrorCS"),sQuery(id+"F0.wireOp",EDGE,"E33.MirrorCS"),sQuery(id+"F0.wireOp",EDGE,"E34.MirrorCS"),sQuery(id+"F0.wireOp",EDGE,"E31.MirrorCS"),sQuery(id+"F0.wireOp",EDGE,"E36.MirrorCS"),sQuery(id+"F0.wireOp",EDGE,"E38.MirrorCS"),sQuery(id+"F0.wireOp",EDGE,"E39.MirrorCS"),sQuery(id+"F0.wireOp",EDGE,"E42.MirrorCS"),sQuery(id+"F0.wireOp",EDGE,"E43.MirrorCS"),sQuery(id+"F0.wireOp",EDGE,"E46"),sQuery(id+"F0.wireOp",EDGE,"E47.MirrorCS"),subQ1,sQuery(id+"F0.wireOp",EDGE,"E49.MirrorCS"),subQ0,sQuery(id+"F0.wireOp",EDGE,"E51")])],"isStart":false}),makeQuery(id+"F1.opExtrude","SWEPT_FACE",FACE,{"disambiguationData":[OSD([subQ1,subQ0])]}),makeQuery(id+"F3.opExtrude","SWEPT_FACE",FACE,{"disambiguationData":[OSD([sQuery(id+"F2.wireOp",EDGE,"E80")])]}),makeQuery(id+"F3.opExtrude","SWEPT_FACE",FACE,{"disambiguationData":[OSD([sQuery(id+"F2.wireOp",EDGE,"E81")])]})])],"derivedFrom":makeQuery(id+"F1.opExtrude","CAP_EDGE",EDGE,{"disambiguationData":[OSD([subQ1,subQ0])],"isStart":false})});}
            var Q22;
            {var subQ0=sQuery(id+"F0.wireOp",EDGE,"E50.MirrorCS");var subQ1=sQuery(id+"F0.wireOp",EDGE,"E48.MirrorCS");Q22=makeQuery(id+"F3.boolean.opBoolean","SPLIT",EDGE,{"disambiguationData":[TD([makeQuery(id+"F1.opExtrude","CAP_FACE",FACE,{"disambiguationData":[OSD([sQuery(id+"F0.wireOp",EDGE,"E15"),sQuery(id+"F0.wireOp",EDGE,"E16"),sQuery(id+"F0.wireOp",EDGE,"E17"),sQuery(id+"F0.wireOp",EDGE,"E20"),sQuery(id+"F0.wireOp",EDGE,"E27.MirrorCS"),sQuery(id+"F0.wireOp",EDGE,"E29.MirrorCS"),sQuery(id+"F0.wireOp",EDGE,"E30.MirrorCS"),sQuery(id+"F0.wireOp",EDGE,"E28.MirrorCS"),sQuery(id+"F0.wireOp",EDGE,"E33.MirrorCS"),sQuery(id+"F0.wireOp",EDGE,"E34.MirrorCS"),sQuery(id+"F0.wireOp",EDGE,"E31.MirrorCS"),sQuery(id+"F0.wireOp",EDGE,"E36.MirrorCS"),sQuery(id+"F0.wireOp",EDGE,"E38.MirrorCS"),sQuery(id+"F0.wireOp",EDGE,"E39.MirrorCS"),sQuery(id+"F0.wireOp",EDGE,"E42.MirrorCS"),sQuery(id+"F0.wireOp",EDGE,"E43.MirrorCS"),sQuery(id+"F0.wireOp",EDGE,"E46"),sQuery(id+"F0.wireOp",EDGE,"E47.MirrorCS"),subQ1,sQuery(id+"F0.wireOp",EDGE,"E49.MirrorCS"),subQ0,sQuery(id+"F0.wireOp",EDGE,"E51")])],"isStart":false}),makeQuery(id+"F1.opExtrude","SWEPT_FACE",FACE,{"disambiguationData":[OSD([subQ1,subQ0])]}),makeQuery(id+"F3.opExtrude","SWEPT_FACE",FACE,{"disambiguationData":[OSD([sQuery(id+"F2.wireOp",EDGE,"E77")])]}),makeQuery(id+"F3.opExtrude","SWEPT_FACE",FACE,{"disambiguationData":[OSD([sQuery(id+"F2.wireOp",EDGE,"E80")])]})])],"derivedFrom":makeQuery(id+"F1.opExtrude","CAP_EDGE",EDGE,{"disambiguationData":[OSD([subQ1,subQ0])],"isStart":false})});}
            var Q23;
            {var subQ0=sQuery(id+"F0.wireOp",EDGE,"E50.MirrorCS");var subQ1=sQuery(id+"F0.wireOp",EDGE,"E48.MirrorCS");Q23=makeQuery(id+"F3.boolean.opBoolean","SPLIT",EDGE,{"disambiguationData":[TD([makeQuery(id+"F1.opExtrude","CAP_FACE",FACE,{"disambiguationData":[OSD([sQuery(id+"F0.wireOp",EDGE,"E15"),sQuery(id+"F0.wireOp",EDGE,"E16"),sQuery(id+"F0.wireOp",EDGE,"E17"),sQuery(id+"F0.wireOp",EDGE,"E20"),sQuery(id+"F0.wireOp",EDGE,"E27.MirrorCS"),sQuery(id+"F0.wireOp",EDGE,"E29.MirrorCS"),sQuery(id+"F0.wireOp",EDGE,"E30.MirrorCS"),sQuery(id+"F0.wireOp",EDGE,"E28.MirrorCS"),sQuery(id+"F0.wireOp",EDGE,"E33.MirrorCS"),sQuery(id+"F0.wireOp",EDGE,"E34.MirrorCS"),sQuery(id+"F0.wireOp",EDGE,"E31.MirrorCS"),sQuery(id+"F0.wireOp",EDGE,"E36.MirrorCS"),sQuery(id+"F0.wireOp",EDGE,"E38.MirrorCS"),sQuery(id+"F0.wireOp",EDGE,"E39.MirrorCS"),sQuery(id+"F0.wireOp",EDGE,"E42.MirrorCS"),sQuery(id+"F0.wireOp",EDGE,"E43.MirrorCS"),sQuery(id+"F0.wireOp",EDGE,"E46"),sQuery(id+"F0.wireOp",EDGE,"E47.MirrorCS"),subQ1,sQuery(id+"F0.wireOp",EDGE,"E49.MirrorCS"),subQ0,sQuery(id+"F0.wireOp",EDGE,"E51")])],"isStart":false}),makeQuery(id+"F1.opExtrude","SWEPT_FACE",FACE,{"disambiguationData":[OSD([subQ1,subQ0])]}),makeQuery(id+"F3.opExtrude","SWEPT_FACE",FACE,{"disambiguationData":[OSD([sQuery(id+"F2.wireOp",EDGE,"E77")])]}),makeQuery(id+"F3.opExtrude","SWEPT_FACE",FACE,{"disambiguationData":[OSD([sQuery(id+"F2.wireOp",EDGE,"E78")])]})])],"derivedFrom":makeQuery(id+"F1.opExtrude","CAP_EDGE",EDGE,{"disambiguationData":[OSD([subQ1,subQ0])],"isStart":false})});}
            var Q24;
            {var subQ0=sQuery(id+"F0.wireOp",EDGE,"E50.MirrorCS");var subQ1=sQuery(id+"F0.wireOp",EDGE,"E48.MirrorCS");Q24=makeQuery(id+"F3.boolean.opBoolean","SPLIT",EDGE,{"disambiguationData":[TD([makeQuery(id+"F1.opExtrude","CAP_FACE",FACE,{"disambiguationData":[OSD([sQuery(id+"F0.wireOp",EDGE,"E15"),sQuery(id+"F0.wireOp",EDGE,"E16"),sQuery(id+"F0.wireOp",EDGE,"E17"),sQuery(id+"F0.wireOp",EDGE,"E20"),sQuery(id+"F0.wireOp",EDGE,"E27.MirrorCS"),sQuery(id+"F0.wireOp",EDGE,"E29.MirrorCS"),sQuery(id+"F0.wireOp",EDGE,"E30.MirrorCS"),sQuery(id+"F0.wireOp",EDGE,"E28.MirrorCS"),sQuery(id+"F0.wireOp",EDGE,"E33.MirrorCS"),sQuery(id+"F0.wireOp",EDGE,"E34.MirrorCS"),sQuery(id+"F0.wireOp",EDGE,"E31.MirrorCS"),sQuery(id+"F0.wireOp",EDGE,"E36.MirrorCS"),sQuery(id+"F0.wireOp",EDGE,"E38.MirrorCS"),sQuery(id+"F0.wireOp",EDGE,"E39.MirrorCS"),sQuery(id+"F0.wireOp",EDGE,"E42.MirrorCS"),sQuery(id+"F0.wireOp",EDGE,"E43.MirrorCS"),sQuery(id+"F0.wireOp",EDGE,"E46"),sQuery(id+"F0.wireOp",EDGE,"E47.MirrorCS"),subQ1,sQuery(id+"F0.wireOp",EDGE,"E49.MirrorCS"),subQ0,sQuery(id+"F0.wireOp",EDGE,"E51")])],"isStart":false}),makeQuery(id+"F1.opExtrude","SWEPT_FACE",FACE,{"disambiguationData":[OSD([subQ1,subQ0])]}),makeQuery(id+"F3.opExtrude","SWEPT_FACE",FACE,{"disambiguationData":[OSD([sQuery(id+"F2.wireOp",EDGE,"E78")])]}),makeQuery(id+"F3.opExtrude","SWEPT_FACE",FACE,{"disambiguationData":[OSD([sQuery(id+"F2.wireOp",EDGE,"E79")])]})])],"derivedFrom":makeQuery(id+"F1.opExtrude","CAP_EDGE",EDGE,{"disambiguationData":[OSD([subQ1,subQ0])],"isStart":false})});}
            var Q25;
            {var subQ0=sQuery(id+"F0.wireOp",EDGE,"E50.MirrorCS");var subQ1=sQuery(id+"F0.wireOp",EDGE,"E48.MirrorCS");Q25=makeQuery(id+"F3.boolean.opBoolean","SPLIT",EDGE,{"disambiguationData":[TD([makeQuery(id+"F1.opExtrude","CAP_FACE",FACE,{"disambiguationData":[OSD([sQuery(id+"F0.wireOp",EDGE,"E15"),sQuery(id+"F0.wireOp",EDGE,"E16"),sQuery(id+"F0.wireOp",EDGE,"E17"),sQuery(id+"F0.wireOp",EDGE,"E20"),sQuery(id+"F0.wireOp",EDGE,"E27.MirrorCS"),sQuery(id+"F0.wireOp",EDGE,"E29.MirrorCS"),sQuery(id+"F0.wireOp",EDGE,"E30.MirrorCS"),sQuery(id+"F0.wireOp",EDGE,"E28.MirrorCS"),sQuery(id+"F0.wireOp",EDGE,"E33.MirrorCS"),sQuery(id+"F0.wireOp",EDGE,"E34.MirrorCS"),sQuery(id+"F0.wireOp",EDGE,"E31.MirrorCS"),sQuery(id+"F0.wireOp",EDGE,"E36.MirrorCS"),sQuery(id+"F0.wireOp",EDGE,"E38.MirrorCS"),sQuery(id+"F0.wireOp",EDGE,"E39.MirrorCS"),sQuery(id+"F0.wireOp",EDGE,"E42.MirrorCS"),sQuery(id+"F0.wireOp",EDGE,"E43.MirrorCS"),sQuery(id+"F0.wireOp",EDGE,"E46"),sQuery(id+"F0.wireOp",EDGE,"E47.MirrorCS"),subQ1,sQuery(id+"F0.wireOp",EDGE,"E49.MirrorCS"),subQ0,sQuery(id+"F0.wireOp",EDGE,"E51")])],"isStart":true}),makeQuery(id+"F1.opExtrude","SWEPT_FACE",FACE,{"disambiguationData":[OSD([subQ1,subQ0])]}),makeQuery(id+"F3.opExtrude","SWEPT_FACE",FACE,{"disambiguationData":[OSD([sQuery(id+"F2.wireOp",EDGE,"E78")])]}),makeQuery(id+"F3.opExtrude","SWEPT_FACE",FACE,{"disambiguationData":[OSD([sQuery(id+"F2.wireOp",EDGE,"E79")])]})])],"derivedFrom":makeQuery(id+"F1.opExtrude","CAP_EDGE",EDGE,{"disambiguationData":[OSD([subQ1,subQ0])],"isStart":true})});}
            var Q26;
            {var subQ0=sQuery(id+"F0.wireOp",EDGE,"E50.MirrorCS");var subQ1=sQuery(id+"F0.wireOp",EDGE,"E48.MirrorCS");Q26=makeQuery(id+"F3.boolean.opBoolean","SPLIT",EDGE,{"disambiguationData":[TD([makeQuery(id+"F1.opExtrude","CAP_FACE",FACE,{"disambiguationData":[OSD([sQuery(id+"F0.wireOp",EDGE,"E15"),sQuery(id+"F0.wireOp",EDGE,"E16"),sQuery(id+"F0.wireOp",EDGE,"E17"),sQuery(id+"F0.wireOp",EDGE,"E20"),sQuery(id+"F0.wireOp",EDGE,"E27.MirrorCS"),sQuery(id+"F0.wireOp",EDGE,"E29.MirrorCS"),sQuery(id+"F0.wireOp",EDGE,"E30.MirrorCS"),sQuery(id+"F0.wireOp",EDGE,"E28.MirrorCS"),sQuery(id+"F0.wireOp",EDGE,"E33.MirrorCS"),sQuery(id+"F0.wireOp",EDGE,"E34.MirrorCS"),sQuery(id+"F0.wireOp",EDGE,"E31.MirrorCS"),sQuery(id+"F0.wireOp",EDGE,"E36.MirrorCS"),sQuery(id+"F0.wireOp",EDGE,"E38.MirrorCS"),sQuery(id+"F0.wireOp",EDGE,"E39.MirrorCS"),sQuery(id+"F0.wireOp",EDGE,"E42.MirrorCS"),sQuery(id+"F0.wireOp",EDGE,"E43.MirrorCS"),sQuery(id+"F0.wireOp",EDGE,"E46"),sQuery(id+"F0.wireOp",EDGE,"E47.MirrorCS"),subQ1,sQuery(id+"F0.wireOp",EDGE,"E49.MirrorCS"),subQ0,sQuery(id+"F0.wireOp",EDGE,"E51")])],"isStart":true}),makeQuery(id+"F1.opExtrude","SWEPT_FACE",FACE,{"disambiguationData":[OSD([subQ1,subQ0])]}),makeQuery(id+"F3.opExtrude","SWEPT_FACE",FACE,{"disambiguationData":[OSD([sQuery(id+"F2.wireOp",EDGE,"E77")])]}),makeQuery(id+"F3.opExtrude","SWEPT_FACE",FACE,{"disambiguationData":[OSD([sQuery(id+"F2.wireOp",EDGE,"E78")])]})])],"derivedFrom":makeQuery(id+"F1.opExtrude","CAP_EDGE",EDGE,{"disambiguationData":[OSD([subQ1,subQ0])],"isStart":true})});}
            var Q27;
            {var subQ0=sQuery(id+"F0.wireOp",EDGE,"E50.MirrorCS");var subQ1=sQuery(id+"F0.wireOp",EDGE,"E48.MirrorCS");Q27=makeQuery(id+"F3.boolean.opBoolean","SPLIT",EDGE,{"disambiguationData":[TD([makeQuery(id+"F1.opExtrude","CAP_FACE",FACE,{"disambiguationData":[OSD([sQuery(id+"F0.wireOp",EDGE,"E15"),sQuery(id+"F0.wireOp",EDGE,"E16"),sQuery(id+"F0.wireOp",EDGE,"E17"),sQuery(id+"F0.wireOp",EDGE,"E20"),sQuery(id+"F0.wireOp",EDGE,"E27.MirrorCS"),sQuery(id+"F0.wireOp",EDGE,"E29.MirrorCS"),sQuery(id+"F0.wireOp",EDGE,"E30.MirrorCS"),sQuery(id+"F0.wireOp",EDGE,"E28.MirrorCS"),sQuery(id+"F0.wireOp",EDGE,"E33.MirrorCS"),sQuery(id+"F0.wireOp",EDGE,"E34.MirrorCS"),sQuery(id+"F0.wireOp",EDGE,"E31.MirrorCS"),sQuery(id+"F0.wireOp",EDGE,"E36.MirrorCS"),sQuery(id+"F0.wireOp",EDGE,"E38.MirrorCS"),sQuery(id+"F0.wireOp",EDGE,"E39.MirrorCS"),sQuery(id+"F0.wireOp",EDGE,"E42.MirrorCS"),sQuery(id+"F0.wireOp",EDGE,"E43.MirrorCS"),sQuery(id+"F0.wireOp",EDGE,"E46"),sQuery(id+"F0.wireOp",EDGE,"E47.MirrorCS"),subQ1,sQuery(id+"F0.wireOp",EDGE,"E49.MirrorCS"),subQ0,sQuery(id+"F0.wireOp",EDGE,"E51")])],"isStart":true}),makeQuery(id+"F1.opExtrude","SWEPT_FACE",FACE,{"disambiguationData":[OSD([subQ1,subQ0])]}),makeQuery(id+"F3.opExtrude","SWEPT_FACE",FACE,{"disambiguationData":[OSD([sQuery(id+"F2.wireOp",EDGE,"E77")])]}),makeQuery(id+"F3.opExtrude","SWEPT_FACE",FACE,{"disambiguationData":[OSD([sQuery(id+"F2.wireOp",EDGE,"E80")])]})])],"derivedFrom":makeQuery(id+"F1.opExtrude","CAP_EDGE",EDGE,{"disambiguationData":[OSD([subQ1,subQ0])],"isStart":true})});}
            var Q28;
            {var subQ0=sQuery(id+"F0.wireOp",EDGE,"E50.MirrorCS");var subQ1=sQuery(id+"F0.wireOp",EDGE,"E48.MirrorCS");Q28=makeQuery(id+"F3.boolean.opBoolean","SPLIT",EDGE,{"disambiguationData":[TD([makeQuery(id+"F1.opExtrude","CAP_FACE",FACE,{"disambiguationData":[OSD([sQuery(id+"F0.wireOp",EDGE,"E15"),sQuery(id+"F0.wireOp",EDGE,"E16"),sQuery(id+"F0.wireOp",EDGE,"E17"),sQuery(id+"F0.wireOp",EDGE,"E20"),sQuery(id+"F0.wireOp",EDGE,"E27.MirrorCS"),sQuery(id+"F0.wireOp",EDGE,"E29.MirrorCS"),sQuery(id+"F0.wireOp",EDGE,"E30.MirrorCS"),sQuery(id+"F0.wireOp",EDGE,"E28.MirrorCS"),sQuery(id+"F0.wireOp",EDGE,"E33.MirrorCS"),sQuery(id+"F0.wireOp",EDGE,"E34.MirrorCS"),sQuery(id+"F0.wireOp",EDGE,"E31.MirrorCS"),sQuery(id+"F0.wireOp",EDGE,"E36.MirrorCS"),sQuery(id+"F0.wireOp",EDGE,"E38.MirrorCS"),sQuery(id+"F0.wireOp",EDGE,"E39.MirrorCS"),sQuery(id+"F0.wireOp",EDGE,"E42.MirrorCS"),sQuery(id+"F0.wireOp",EDGE,"E43.MirrorCS"),sQuery(id+"F0.wireOp",EDGE,"E46"),sQuery(id+"F0.wireOp",EDGE,"E47.MirrorCS"),subQ1,sQuery(id+"F0.wireOp",EDGE,"E49.MirrorCS"),subQ0,sQuery(id+"F0.wireOp",EDGE,"E51")])],"isStart":true}),makeQuery(id+"F1.opExtrude","SWEPT_FACE",FACE,{"disambiguationData":[OSD([subQ1,subQ0])]}),makeQuery(id+"F3.opExtrude","SWEPT_FACE",FACE,{"disambiguationData":[OSD([sQuery(id+"F2.wireOp",EDGE,"E80")])]}),makeQuery(id+"F3.opExtrude","SWEPT_FACE",FACE,{"disambiguationData":[OSD([sQuery(id+"F2.wireOp",EDGE,"E81")])]})])],"derivedFrom":makeQuery(id+"F1.opExtrude","CAP_EDGE",EDGE,{"disambiguationData":[OSD([subQ1,subQ0])],"isStart":true})});}
            var Q29;
            {var subQ0=sQuery(id+"F0.wireOp",EDGE,"E50.MirrorCS");var subQ1=sQuery(id+"F0.wireOp",EDGE,"E48.MirrorCS");Q29=makeQuery(id+"F3.boolean.opBoolean","SPLIT",EDGE,{"disambiguationData":[TD([makeQuery(id+"F1.opExtrude","CAP_FACE",FACE,{"disambiguationData":[OSD([sQuery(id+"F0.wireOp",EDGE,"E15"),sQuery(id+"F0.wireOp",EDGE,"E16"),sQuery(id+"F0.wireOp",EDGE,"E17"),sQuery(id+"F0.wireOp",EDGE,"E20"),sQuery(id+"F0.wireOp",EDGE,"E27.MirrorCS"),sQuery(id+"F0.wireOp",EDGE,"E29.MirrorCS"),sQuery(id+"F0.wireOp",EDGE,"E30.MirrorCS"),sQuery(id+"F0.wireOp",EDGE,"E28.MirrorCS"),sQuery(id+"F0.wireOp",EDGE,"E33.MirrorCS"),sQuery(id+"F0.wireOp",EDGE,"E34.MirrorCS"),sQuery(id+"F0.wireOp",EDGE,"E31.MirrorCS"),sQuery(id+"F0.wireOp",EDGE,"E36.MirrorCS"),sQuery(id+"F0.wireOp",EDGE,"E38.MirrorCS"),sQuery(id+"F0.wireOp",EDGE,"E39.MirrorCS"),sQuery(id+"F0.wireOp",EDGE,"E42.MirrorCS"),sQuery(id+"F0.wireOp",EDGE,"E43.MirrorCS"),sQuery(id+"F0.wireOp",EDGE,"E46"),sQuery(id+"F0.wireOp",EDGE,"E47.MirrorCS"),subQ1,sQuery(id+"F0.wireOp",EDGE,"E49.MirrorCS"),subQ0,sQuery(id+"F0.wireOp",EDGE,"E51")])],"isStart":true}),makeQuery(id+"F1.opExtrude","SWEPT_FACE",FACE,{"disambiguationData":[OSD([subQ1,subQ0])]}),makeQuery(id+"F3.opExtrude","SWEPT_FACE",FACE,{"disambiguationData":[OSD([sQuery(id+"F2.wireOp",EDGE,"E81")])]}),makeQuery(id+"F3.opExtrude","SWEPT_FACE",FACE,{"disambiguationData":[OSD([sQuery(id+"F2.wireOp",EDGE,"E82")])]})])],"derivedFrom":makeQuery(id+"F1.opExtrude","CAP_EDGE",EDGE,{"disambiguationData":[OSD([subQ1,subQ0])],"isStart":true})});}
            fillet(context, id + "F5", {"entities" : qUnion([Q0, Q1, Q2, Q3, Q4, Q5, Q6, Q7, Q8, Q9, Q10, Q11, Q12, Q13, Q14, Q15, Q16, Q17, Q18, Q19, Q20, Q21, Q22, Q23, Q24, Q25, Q26, Q27, Q28, Q29]), "radius" : 1.27 * mm, "tangentPropagation" : true, "allowEdgeOverflow" : false});
        }
    });
